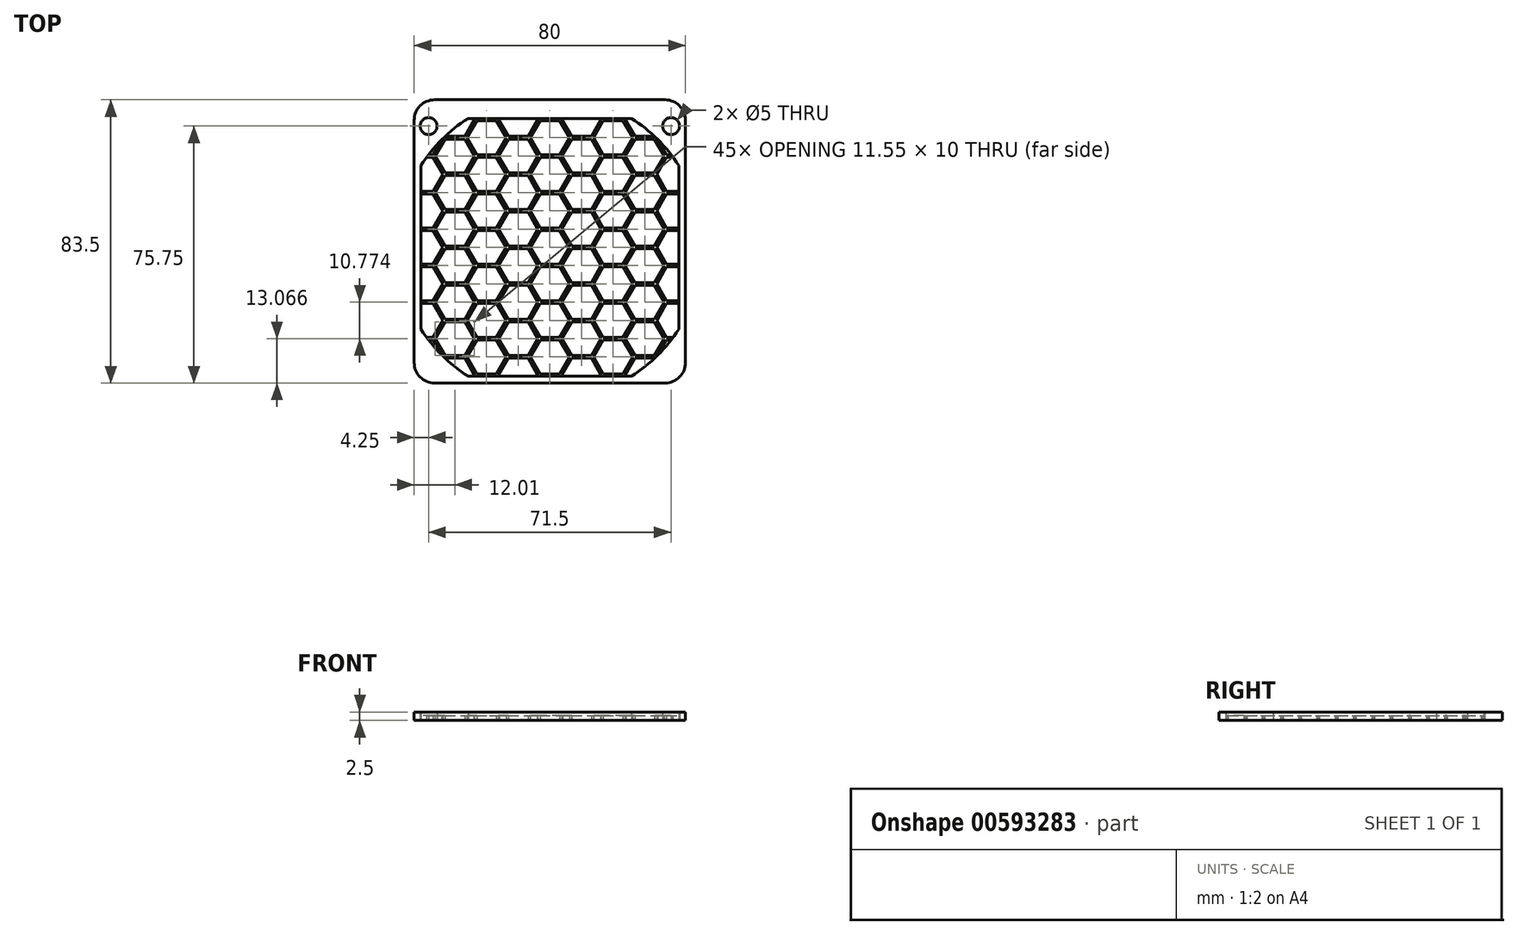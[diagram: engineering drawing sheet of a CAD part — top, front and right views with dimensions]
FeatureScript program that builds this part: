
annotation { "Feature Type Name" : "Feature", "Feature Type Description" : "" }
export const myFeature = defineFeature(function(context is Context, id is Id, definition is map)
    precondition{}
    {
        {
            var Q0;
            Q0=qCreatedBy(makeId("Top.planeOp"),FACE);
            var sketch = newSketch(context, id + "F0", { "sketchPlane" : qUnion([Q0]), "disableImprinting" : false});
            skPoint(sketch, "E0.1.2.4", {"position": v(-32.32, -29.43) * mm});
            skLineSegment(sketch, "E0.1.2.6", {"start": v(-35.76, -27.32) * mm, "end": v(-34.43, -27.32) * mm});
            skLineSegment(sketch, "E0.1.2.10", {"start": v(-34.43, -27.32) * mm, "end": v(-31.86, -31.78) * mm});
            skPoint(sketch, "E0.1.3.1", {"position": v(-37.32, -21.55) * mm});
            skPoint(sketch, "E0.1.3.4", {"position": v(-32.32, -18.66) * mm});
            skLineSegment(sketch, "E0.1.3.6", {"start": v(-38, -16.55) * mm, "end": v(-34.43, -16.55) * mm});
            skLineSegment(sketch, "E0.1.3.10", {"start": v(-34.43, -16.55) * mm, "end": v(-31.55, -21.55) * mm});
            skLineSegment(sketch, "E0.1.3.13", {"start": v(-31.55, -21.55) * mm, "end": v(-34.43, -26.55) * mm});
            skLineSegment(sketch, "E0.1.3.16", {"start": v(-34.43, -26.55) * mm, "end": v(-36.34, -26.55) * mm});
            skPoint(sketch, "E0.1.3.18", {"position": v(-37.32, -16.55) * mm});
            skPoint(sketch, "E0.1.4.1", {"position": v(-37.32, -10.77) * mm});
            skPoint(sketch, "E0.1.4.4", {"position": v(-32.32, -7.89) * mm});
            skLineSegment(sketch, "E0.1.4.6", {"start": v(-38, -5.77) * mm, "end": v(-34.43, -5.77) * mm});
            skLineSegment(sketch, "E0.1.4.10", {"start": v(-34.43, -5.77) * mm, "end": v(-31.55, -10.77) * mm});
            skLineSegment(sketch, "E0.1.4.13", {"start": v(-31.55, -10.77) * mm, "end": v(-34.43, -15.77) * mm});
            skLineSegment(sketch, "E0.1.4.16", {"start": v(-34.43, -15.77) * mm, "end": v(-38, -15.77) * mm});
            skPoint(sketch, "E0.1.4.18", {"position": v(-37.32, -5.77) * mm});
            skPoint(sketch, "E0.1.5.1", {"position": v(-37.32, 0) * mm});
            skPoint(sketch, "E0.1.5.4", {"position": v(-32.32, 2.89) * mm});
            skLineSegment(sketch, "E0.1.5.6", {"start": v(-38, 5) * mm, "end": v(-34.43, 5) * mm});
            skLineSegment(sketch, "E0.1.5.10", {"start": v(-34.43, 5) * mm, "end": v(-31.55, 0) * mm});
            skLineSegment(sketch, "E0.1.5.13", {"start": v(-31.55, 0) * mm, "end": v(-34.43, -5) * mm});
            skLineSegment(sketch, "E0.1.5.16", {"start": v(-34.43, -5) * mm, "end": v(-38, -5) * mm});
            skPoint(sketch, "E0.1.5.18", {"position": v(-37.32, 5) * mm});
            skPoint(sketch, "E0.1.6.1", {"position": v(-37.32, 10.77) * mm});
            skPoint(sketch, "E0.1.6.4", {"position": v(-32.32, 13.66) * mm});
            skLineSegment(sketch, "E0.1.6.6", {"start": v(-38, 15.77) * mm, "end": v(-34.43, 15.77) * mm});
            skLineSegment(sketch, "E0.1.6.10", {"start": v(-34.43, 15.77) * mm, "end": v(-31.55, 10.77) * mm});
            skLineSegment(sketch, "E0.1.6.13", {"start": v(-31.55, 10.77) * mm, "end": v(-34.43, 5.77) * mm});
            skLineSegment(sketch, "E0.1.6.16", {"start": v(-34.43, 5.77) * mm, "end": v(-38, 5.77) * mm});
            skPoint(sketch, "E0.1.6.18", {"position": v(-37.32, 15.77) * mm});
            skPoint(sketch, "E0.1.7.1", {"position": v(-37.32, 21.55) * mm});
            skPoint(sketch, "E0.1.7.4", {"position": v(-32.32, 24.43) * mm});
            skLineSegment(sketch, "E0.1.7.6", {"start": v(-36.34, 26.55) * mm, "end": v(-34.43, 26.55) * mm});
            skLineSegment(sketch, "E0.1.7.10", {"start": v(-34.43, 26.55) * mm, "end": v(-31.55, 21.55) * mm});
            skLineSegment(sketch, "E0.1.7.13", {"start": v(-31.55, 21.55) * mm, "end": v(-34.43, 16.55) * mm});
            skLineSegment(sketch, "E0.1.7.16", {"start": v(-34.43, 16.55) * mm, "end": v(-38, 16.55) * mm});
            skLineSegment(sketch, "E0.1.8.13", {"start": v(-31.86, 31.78) * mm, "end": v(-34.43, 27.32) * mm});
            skLineSegment(sketch, "E0.1.8.16", {"start": v(-34.43, 27.32) * mm, "end": v(-35.76, 27.32) * mm});
            skPoint(sketch, "E0.2.1.18", {"position": v(-18.66, -38.1) * mm});
            skLineSegment(sketch, "E0.2.2.0", {"start": v(-24.43, -32.32) * mm, "end": v(-21.55, -27.32) * mm});
            skPoint(sketch, "E0.2.2.1", {"position": v(-18.66, -32.32) * mm});
            skLineSegment(sketch, "E0.2.2.3", {"start": v(-25.1, -32.7) * mm, "end": v(-22.22, -37.7) * mm});
            skPoint(sketch, "E0.2.2.4", {"position": v(-13.66, -29.43) * mm});
            skLineSegment(sketch, "E0.2.2.5", {"start": v(-30.9, -32.7) * mm, "end": v(-25.1, -32.7) * mm});
            skLineSegment(sketch, "E0.2.2.6", {"start": v(-21.55, -27.32) * mm, "end": v(-15.77, -27.32) * mm});
            skLineSegment(sketch, "E0.2.2.10", {"start": v(-15.77, -27.32) * mm, "end": v(-12.89, -32.32) * mm});
            skLineSegment(sketch, "E0.2.2.12", {"start": v(-22.22, -37.7) * mm, "end": v(-22.39, -38) * mm});
            skLineSegment(sketch, "E0.2.2.13", {"start": v(-12.89, -32.32) * mm, "end": v(-15.77, -37.32) * mm});
            skPoint(sketch, "E0.2.2.14", {"position": v(-23, -34.82) * mm});
            skLineSegment(sketch, "E0.2.2.15", {"start": v(-21.55, -37.32) * mm, "end": v(-24.43, -32.32) * mm});
            skLineSegment(sketch, "E0.2.2.16", {"start": v(-15.77, -37.32) * mm, "end": v(-21.55, -37.32) * mm});
            skPoint(sketch, "E0.2.2.17", {"position": v(-28, -32.7) * mm});
            skPoint(sketch, "E0.2.2.18", {"position": v(-18.66, -27.32) * mm});
            skPoint(sketch, "E0.2.2.19", {"position": v(-23, -34.82) * mm});
            skLineSegment(sketch, "E0.2.3.0", {"start": v(-24.43, -21.55) * mm, "end": v(-21.55, -16.55) * mm});
            skPoint(sketch, "E0.2.3.1", {"position": v(-18.66, -21.55) * mm});
            skPoint(sketch, "E0.2.3.2", {"position": v(-28, -26.93) * mm});
            skLineSegment(sketch, "E0.2.3.3", {"start": v(-25.1, -21.93) * mm, "end": v(-22.22, -26.93) * mm});
            skPoint(sketch, "E0.2.3.4", {"position": v(-13.66, -18.66) * mm});
            skLineSegment(sketch, "E0.2.3.5", {"start": v(-30.88, -21.93) * mm, "end": v(-25.1, -21.93) * mm});
            skLineSegment(sketch, "E0.2.3.6", {"start": v(-21.55, -16.55) * mm, "end": v(-15.77, -16.55) * mm});
            skLineSegment(sketch, "E0.2.3.7", {"start": v(-25.1, -31.93) * mm, "end": v(-30.88, -31.93) * mm});
            skPoint(sketch, "E0.2.3.8", {"position": v(-32.32, -29.43) * mm});
            skLineSegment(sketch, "E0.2.3.9", {"start": v(-30.88, -31.93) * mm, "end": v(-33.76, -26.93) * mm});
            skLineSegment(sketch, "E0.2.3.10", {"start": v(-15.77, -16.55) * mm, "end": v(-12.89, -21.55) * mm});
            skLineSegment(sketch, "E0.2.3.11", {"start": v(-33.76, -26.93) * mm, "end": v(-30.88, -21.93) * mm});
            skLineSegment(sketch, "E0.2.3.12", {"start": v(-22.22, -26.93) * mm, "end": v(-25.1, -31.93) * mm});
            skLineSegment(sketch, "E0.2.3.13", {"start": v(-12.89, -21.55) * mm, "end": v(-15.77, -26.55) * mm});
            skPoint(sketch, "E0.2.3.14", {"position": v(-23, -24.05) * mm});
            skLineSegment(sketch, "E0.2.3.15", {"start": v(-21.55, -26.55) * mm, "end": v(-24.43, -21.55) * mm});
            skLineSegment(sketch, "E0.2.3.16", {"start": v(-15.77, -26.55) * mm, "end": v(-21.55, -26.55) * mm});
            skPoint(sketch, "E0.2.3.17", {"position": v(-28, -21.93) * mm});
            skPoint(sketch, "E0.2.3.18", {"position": v(-18.66, -16.55) * mm});
            skPoint(sketch, "E0.2.3.19", {"position": v(-23, -24.05) * mm});
            skLineSegment(sketch, "E0.2.4.0", {"start": v(-24.43, -10.77) * mm, "end": v(-21.55, -5.77) * mm});
            skPoint(sketch, "E0.2.4.1", {"position": v(-18.66, -10.77) * mm});
            skPoint(sketch, "E0.2.4.2", {"position": v(-28, -16.16) * mm});
            skLineSegment(sketch, "E0.2.4.3", {"start": v(-25.1, -11.16) * mm, "end": v(-22.22, -16.16) * mm});
            skPoint(sketch, "E0.2.4.4", {"position": v(-13.66, -7.89) * mm});
            skLineSegment(sketch, "E0.2.4.5", {"start": v(-30.88, -11.16) * mm, "end": v(-25.1, -11.16) * mm});
            skLineSegment(sketch, "E0.2.4.6", {"start": v(-21.55, -5.77) * mm, "end": v(-15.77, -5.77) * mm});
            skLineSegment(sketch, "E0.2.4.7", {"start": v(-25.1, -21.16) * mm, "end": v(-30.88, -21.16) * mm});
            skPoint(sketch, "E0.2.4.8", {"position": v(-32.32, -18.66) * mm});
            skLineSegment(sketch, "E0.2.4.9", {"start": v(-30.88, -21.16) * mm, "end": v(-33.76, -16.16) * mm});
            skLineSegment(sketch, "E0.2.4.10", {"start": v(-15.77, -5.77) * mm, "end": v(-12.89, -10.77) * mm});
            skLineSegment(sketch, "E0.2.4.11", {"start": v(-33.76, -16.16) * mm, "end": v(-30.88, -11.16) * mm});
            skLineSegment(sketch, "E0.2.4.12", {"start": v(-22.22, -16.16) * mm, "end": v(-25.1, -21.16) * mm});
            skLineSegment(sketch, "E0.2.4.13", {"start": v(-12.89, -10.77) * mm, "end": v(-15.77, -15.77) * mm});
            skPoint(sketch, "E0.2.4.14", {"position": v(-23, -13.27) * mm});
            skLineSegment(sketch, "E0.2.4.15", {"start": v(-21.55, -15.77) * mm, "end": v(-24.43, -10.77) * mm});
            skLineSegment(sketch, "E0.2.4.16", {"start": v(-15.77, -15.77) * mm, "end": v(-21.55, -15.77) * mm});
            skPoint(sketch, "E0.2.4.17", {"position": v(-28, -11.16) * mm});
            skPoint(sketch, "E0.2.4.18", {"position": v(-18.66, -5.77) * mm});
            skPoint(sketch, "E0.2.4.19", {"position": v(-23, -13.27) * mm});
            skLineSegment(sketch, "E0.2.5.0", {"start": v(-24.43, 0) * mm, "end": v(-21.55, 5) * mm});
            skPoint(sketch, "E0.2.5.1", {"position": v(-18.66, 0) * mm});
            skPoint(sketch, "E0.2.5.2", {"position": v(-28, -5.39) * mm});
            skLineSegment(sketch, "E0.2.5.3", {"start": v(-25.1, -0.39) * mm, "end": v(-22.22, -5.39) * mm});
            skPoint(sketch, "E0.2.5.4", {"position": v(-13.66, 2.89) * mm});
            skLineSegment(sketch, "E0.2.5.5", {"start": v(-30.88, -0.39) * mm, "end": v(-25.1, -0.39) * mm});
            skLineSegment(sketch, "E0.2.5.6", {"start": v(-21.55, 5) * mm, "end": v(-15.77, 5) * mm});
            skLineSegment(sketch, "E0.2.5.7", {"start": v(-25.1, -10.39) * mm, "end": v(-30.88, -10.39) * mm});
            skPoint(sketch, "E0.2.5.8", {"position": v(-32.32, -7.89) * mm});
            skLineSegment(sketch, "E0.2.5.9", {"start": v(-30.88, -10.39) * mm, "end": v(-33.76, -5.39) * mm});
            skLineSegment(sketch, "E0.2.5.10", {"start": v(-15.77, 5) * mm, "end": v(-12.89, 0) * mm});
            skLineSegment(sketch, "E0.2.5.11", {"start": v(-33.76, -5.39) * mm, "end": v(-30.88, -0.39) * mm});
            skLineSegment(sketch, "E0.2.5.12", {"start": v(-22.22, -5.39) * mm, "end": v(-25.1, -10.39) * mm});
            skLineSegment(sketch, "E0.2.5.13", {"start": v(-12.89, 0) * mm, "end": v(-15.77, -5) * mm});
            skPoint(sketch, "E0.2.5.14", {"position": v(-23, -2.5) * mm});
            skLineSegment(sketch, "E0.2.5.15", {"start": v(-21.55, -5) * mm, "end": v(-24.43, 0) * mm});
            skLineSegment(sketch, "E0.2.5.16", {"start": v(-15.77, -5) * mm, "end": v(-21.55, -5) * mm});
            skPoint(sketch, "E0.2.5.17", {"position": v(-28, -0.39) * mm});
            skPoint(sketch, "E0.2.5.18", {"position": v(-18.66, 5) * mm});
            skPoint(sketch, "E0.2.5.19", {"position": v(-23, -2.5) * mm});
            skLineSegment(sketch, "E0.2.6.0", {"start": v(-24.43, 10.77) * mm, "end": v(-21.55, 15.77) * mm});
            skPoint(sketch, "E0.2.6.1", {"position": v(-18.66, 10.77) * mm});
            skPoint(sketch, "E0.2.6.2", {"position": v(-28, 5.39) * mm});
            skLineSegment(sketch, "E0.2.6.3", {"start": v(-25.1, 10.39) * mm, "end": v(-22.22, 5.39) * mm});
            skPoint(sketch, "E0.2.6.4", {"position": v(-13.66, 13.66) * mm});
            skLineSegment(sketch, "E0.2.6.5", {"start": v(-30.88, 10.39) * mm, "end": v(-25.1, 10.39) * mm});
            skLineSegment(sketch, "E0.2.6.6", {"start": v(-21.55, 15.77) * mm, "end": v(-15.77, 15.77) * mm});
            skLineSegment(sketch, "E0.2.6.7", {"start": v(-25.1, 0.39) * mm, "end": v(-30.88, 0.39) * mm});
            skPoint(sketch, "E0.2.6.8", {"position": v(-32.32, 2.89) * mm});
            skLineSegment(sketch, "E0.2.6.9", {"start": v(-30.88, 0.39) * mm, "end": v(-33.76, 5.39) * mm});
            skLineSegment(sketch, "E0.2.6.10", {"start": v(-15.77, 15.77) * mm, "end": v(-12.89, 10.77) * mm});
            skLineSegment(sketch, "E0.2.6.11", {"start": v(-33.76, 5.39) * mm, "end": v(-30.88, 10.39) * mm});
            skLineSegment(sketch, "E0.2.6.12", {"start": v(-22.22, 5.39) * mm, "end": v(-25.1, 0.39) * mm});
            skLineSegment(sketch, "E0.2.6.13", {"start": v(-12.89, 10.77) * mm, "end": v(-15.77, 5.77) * mm});
            skPoint(sketch, "E0.2.6.14", {"position": v(-23, 8.27) * mm});
            skLineSegment(sketch, "E0.2.6.15", {"start": v(-21.55, 5.77) * mm, "end": v(-24.43, 10.77) * mm});
            skLineSegment(sketch, "E0.2.6.16", {"start": v(-15.77, 5.77) * mm, "end": v(-21.55, 5.77) * mm});
            skPoint(sketch, "E0.2.6.17", {"position": v(-28, 10.39) * mm});
            skPoint(sketch, "E0.2.6.18", {"position": v(-18.66, 15.77) * mm});
            skPoint(sketch, "E0.2.6.19", {"position": v(-23, 8.27) * mm});
            skLineSegment(sketch, "E0.2.7.0", {"start": v(-24.43, 21.55) * mm, "end": v(-21.55, 26.55) * mm});
            skPoint(sketch, "E0.2.7.1", {"position": v(-18.66, 21.55) * mm});
            skPoint(sketch, "E0.2.7.2", {"position": v(-28, 16.16) * mm});
            skLineSegment(sketch, "E0.2.7.3", {"start": v(-25.1, 21.16) * mm, "end": v(-22.22, 16.16) * mm});
            skPoint(sketch, "E0.2.7.4", {"position": v(-13.66, 24.43) * mm});
            skLineSegment(sketch, "E0.2.7.5", {"start": v(-30.88, 21.16) * mm, "end": v(-25.1, 21.16) * mm});
            skLineSegment(sketch, "E0.2.7.6", {"start": v(-21.55, 26.55) * mm, "end": v(-15.77, 26.55) * mm});
            skLineSegment(sketch, "E0.2.7.7", {"start": v(-25.1, 11.16) * mm, "end": v(-30.88, 11.16) * mm});
            skPoint(sketch, "E0.2.7.8", {"position": v(-32.32, 13.66) * mm});
            skLineSegment(sketch, "E0.2.7.9", {"start": v(-30.88, 11.16) * mm, "end": v(-33.76, 16.16) * mm});
            skLineSegment(sketch, "E0.2.7.10", {"start": v(-15.77, 26.55) * mm, "end": v(-12.89, 21.55) * mm});
            skLineSegment(sketch, "E0.2.7.11", {"start": v(-33.76, 16.16) * mm, "end": v(-30.88, 21.16) * mm});
            skLineSegment(sketch, "E0.2.7.12", {"start": v(-22.22, 16.16) * mm, "end": v(-25.1, 11.16) * mm});
            skLineSegment(sketch, "E0.2.7.13", {"start": v(-12.89, 21.55) * mm, "end": v(-15.77, 16.55) * mm});
            skPoint(sketch, "E0.2.7.14", {"position": v(-23, 19.05) * mm});
            skLineSegment(sketch, "E0.2.7.15", {"start": v(-21.55, 16.55) * mm, "end": v(-24.43, 21.55) * mm});
            skLineSegment(sketch, "E0.2.7.16", {"start": v(-15.77, 16.55) * mm, "end": v(-21.55, 16.55) * mm});
            skPoint(sketch, "E0.2.7.17", {"position": v(-28, 21.16) * mm});
            skPoint(sketch, "E0.2.7.18", {"position": v(-18.66, 26.55) * mm});
            skPoint(sketch, "E0.2.7.19", {"position": v(-23, 19.05) * mm});
            skLineSegment(sketch, "E0.2.8.0", {"start": v(-24.43, 32.32) * mm, "end": v(-21.55, 37.32) * mm});
            skPoint(sketch, "E0.2.8.1", {"position": v(-18.66, 32.32) * mm});
            skPoint(sketch, "E0.2.8.2", {"position": v(-28, 26.93) * mm});
            skLineSegment(sketch, "E0.2.8.3", {"start": v(-25.1, 31.93) * mm, "end": v(-22.22, 26.93) * mm});
            skPoint(sketch, "E0.2.8.4", {"position": v(-13.66, 35.2) * mm});
            skLineSegment(sketch, "E0.2.8.5", {"start": v(-30.88, 31.93) * mm, "end": v(-25.1, 31.93) * mm});
            skLineSegment(sketch, "E0.2.8.6", {"start": v(-21.55, 37.32) * mm, "end": v(-15.77, 37.32) * mm});
            skLineSegment(sketch, "E0.2.8.7", {"start": v(-25.1, 21.93) * mm, "end": v(-30.88, 21.93) * mm});
            skPoint(sketch, "E0.2.8.8", {"position": v(-32.32, 24.43) * mm});
            skLineSegment(sketch, "E0.2.8.9", {"start": v(-30.88, 21.93) * mm, "end": v(-33.76, 26.93) * mm});
            skLineSegment(sketch, "E0.2.8.10", {"start": v(-15.77, 37.32) * mm, "end": v(-12.89, 32.32) * mm});
            skLineSegment(sketch, "E0.2.8.11", {"start": v(-33.76, 26.93) * mm, "end": v(-30.88, 31.93) * mm});
            skLineSegment(sketch, "E0.2.8.12", {"start": v(-22.22, 26.93) * mm, "end": v(-25.1, 21.93) * mm});
            skLineSegment(sketch, "E0.2.8.13", {"start": v(-12.89, 32.32) * mm, "end": v(-15.77, 27.32) * mm});
            skPoint(sketch, "E0.2.8.14", {"position": v(-23, 29.82) * mm});
            skLineSegment(sketch, "E0.2.8.15", {"start": v(-21.55, 27.32) * mm, "end": v(-24.43, 32.32) * mm});
            skLineSegment(sketch, "E0.2.8.16", {"start": v(-15.77, 27.32) * mm, "end": v(-21.55, 27.32) * mm});
            skPoint(sketch, "E0.2.8.17", {"position": v(-28, 31.93) * mm});
            skPoint(sketch, "E0.2.8.18", {"position": v(-18.66, 37.32) * mm});
            skPoint(sketch, "E0.2.8.19", {"position": v(-23, 29.82) * mm});
            skLineSegment(sketch, "E0.2.9.3", {"start": v(-22.39, 38) * mm, "end": v(-22.22, 37.7) * mm});
            skLineSegment(sketch, "E0.2.9.7", {"start": v(-25.1, 32.7) * mm, "end": v(-30.9, 32.7) * mm});
            skLineSegment(sketch, "E0.2.9.12", {"start": v(-22.22, 37.7) * mm, "end": v(-25.1, 32.7) * mm});
            skPoint(sketch, "E0.3.1.18", {"position": v(0, -38.1) * mm});
            skLineSegment(sketch, "E0.3.2.0", {"start": v(-5.77, -32.32) * mm, "end": v(-2.89, -27.32) * mm});
            skPoint(sketch, "E0.3.2.1", {"position": v(0, -32.32) * mm});
            skPoint(sketch, "E0.3.2.2", {"position": v(-9.33, -37.7) * mm});
            skLineSegment(sketch, "E0.3.2.3", {"start": v(-6.44, -32.7) * mm, "end": v(-3.56, -37.7) * mm});
            skPoint(sketch, "E0.3.2.4", {"position": v(5, -29.43) * mm});
            skLineSegment(sketch, "E0.3.2.5", {"start": v(-12.22, -32.7) * mm, "end": v(-6.44, -32.7) * mm});
            skLineSegment(sketch, "E0.3.2.6", {"start": v(-2.89, -27.32) * mm, "end": v(2.89, -27.32) * mm});
            skLineSegment(sketch, "E0.3.2.9", {"start": v(-14.93, -38) * mm, "end": v(-15.1, -37.7) * mm});
            skLineSegment(sketch, "E0.3.2.10", {"start": v(2.89, -27.32) * mm, "end": v(5.77, -32.32) * mm});
            skLineSegment(sketch, "E0.3.2.11", {"start": v(-15.1, -37.7) * mm, "end": v(-12.22, -32.7) * mm});
            skLineSegment(sketch, "E0.3.2.12", {"start": v(-3.56, -37.7) * mm, "end": v(-3.73, -38) * mm});
            skLineSegment(sketch, "E0.3.2.13", {"start": v(5.77, -32.32) * mm, "end": v(2.89, -37.32) * mm});
            skPoint(sketch, "E0.3.2.14", {"position": v(-4.33, -34.82) * mm});
            skLineSegment(sketch, "E0.3.2.15", {"start": v(-2.89, -37.32) * mm, "end": v(-5.77, -32.32) * mm});
            skLineSegment(sketch, "E0.3.2.16", {"start": v(2.89, -37.32) * mm, "end": v(-2.89, -37.32) * mm});
            skPoint(sketch, "E0.3.2.17", {"position": v(-9.33, -32.7) * mm});
            skPoint(sketch, "E0.3.2.18", {"position": v(0, -27.32) * mm});
            skPoint(sketch, "E0.3.2.19", {"position": v(-4.33, -34.82) * mm});
            skLineSegment(sketch, "E0.3.3.0", {"start": v(-5.77, -21.55) * mm, "end": v(-2.89, -16.55) * mm});
            skPoint(sketch, "E0.3.3.1", {"position": v(0, -21.55) * mm});
            skPoint(sketch, "E0.3.3.2", {"position": v(-9.33, -26.93) * mm});
            skLineSegment(sketch, "E0.3.3.3", {"start": v(-6.44, -21.93) * mm, "end": v(-3.56, -26.93) * mm});
            skPoint(sketch, "E0.3.3.4", {"position": v(5, -18.66) * mm});
            skLineSegment(sketch, "E0.3.3.5", {"start": v(-12.22, -21.93) * mm, "end": v(-6.44, -21.93) * mm});
            skLineSegment(sketch, "E0.3.3.6", {"start": v(-2.89, -16.55) * mm, "end": v(2.89, -16.55) * mm});
            skLineSegment(sketch, "E0.3.3.7", {"start": v(-6.44, -31.93) * mm, "end": v(-12.22, -31.93) * mm});
            skPoint(sketch, "E0.3.3.8", {"position": v(-13.66, -29.43) * mm});
            skLineSegment(sketch, "E0.3.3.9", {"start": v(-12.22, -31.93) * mm, "end": v(-15.1, -26.93) * mm});
            skLineSegment(sketch, "E0.3.3.10", {"start": v(2.89, -16.55) * mm, "end": v(5.77, -21.55) * mm});
            skLineSegment(sketch, "E0.3.3.11", {"start": v(-15.1, -26.93) * mm, "end": v(-12.22, -21.93) * mm});
            skLineSegment(sketch, "E0.3.3.12", {"start": v(-3.56, -26.93) * mm, "end": v(-6.44, -31.93) * mm});
            skLineSegment(sketch, "E0.3.3.13", {"start": v(5.77, -21.55) * mm, "end": v(2.89, -26.55) * mm});
            skPoint(sketch, "E0.3.3.14", {"position": v(-4.33, -24.05) * mm});
            skLineSegment(sketch, "E0.3.3.15", {"start": v(-2.89, -26.55) * mm, "end": v(-5.77, -21.55) * mm});
            skLineSegment(sketch, "E0.3.3.16", {"start": v(2.89, -26.55) * mm, "end": v(-2.89, -26.55) * mm});
            skPoint(sketch, "E0.3.3.17", {"position": v(-9.33, -21.93) * mm});
            skPoint(sketch, "E0.3.3.18", {"position": v(0, -16.55) * mm});
            skPoint(sketch, "E0.3.3.19", {"position": v(-4.33, -24.05) * mm});
            skLineSegment(sketch, "E0.3.4.0", {"start": v(-5.77, -10.77) * mm, "end": v(-2.89, -5.77) * mm});
            skPoint(sketch, "E0.3.4.1", {"position": v(0, -10.77) * mm});
            skPoint(sketch, "E0.3.4.2", {"position": v(-9.33, -16.16) * mm});
            skLineSegment(sketch, "E0.3.4.3", {"start": v(-6.44, -11.16) * mm, "end": v(-3.56, -16.16) * mm});
            skPoint(sketch, "E0.3.4.4", {"position": v(5, -7.89) * mm});
            skLineSegment(sketch, "E0.3.4.5", {"start": v(-12.22, -11.16) * mm, "end": v(-6.44, -11.16) * mm});
            skLineSegment(sketch, "E0.3.4.6", {"start": v(-2.89, -5.77) * mm, "end": v(2.89, -5.77) * mm});
            skLineSegment(sketch, "E0.3.4.7", {"start": v(-6.44, -21.16) * mm, "end": v(-12.22, -21.16) * mm});
            skPoint(sketch, "E0.3.4.8", {"position": v(-13.66, -18.66) * mm});
            skLineSegment(sketch, "E0.3.4.9", {"start": v(-12.22, -21.16) * mm, "end": v(-15.1, -16.16) * mm});
            skLineSegment(sketch, "E0.3.4.10", {"start": v(2.89, -5.77) * mm, "end": v(5.77, -10.77) * mm});
            skLineSegment(sketch, "E0.3.4.11", {"start": v(-15.1, -16.16) * mm, "end": v(-12.22, -11.16) * mm});
            skLineSegment(sketch, "E0.3.4.12", {"start": v(-3.56, -16.16) * mm, "end": v(-6.44, -21.16) * mm});
            skLineSegment(sketch, "E0.3.4.13", {"start": v(5.77, -10.77) * mm, "end": v(2.89, -15.77) * mm});
            skPoint(sketch, "E0.3.4.14", {"position": v(-4.33, -13.27) * mm});
            skLineSegment(sketch, "E0.3.4.15", {"start": v(-2.89, -15.77) * mm, "end": v(-5.77, -10.77) * mm});
            skLineSegment(sketch, "E0.3.4.16", {"start": v(2.89, -15.77) * mm, "end": v(-2.89, -15.77) * mm});
            skPoint(sketch, "E0.3.4.17", {"position": v(-9.33, -11.16) * mm});
            skPoint(sketch, "E0.3.4.18", {"position": v(0, -5.77) * mm});
            skPoint(sketch, "E0.3.4.19", {"position": v(-4.33, -13.27) * mm});
            skLineSegment(sketch, "E0.3.5.0", {"start": v(-5.77, 0) * mm, "end": v(-2.89, 5) * mm});
            skPoint(sketch, "E0.3.5.1", {"position": v(0, 0) * mm});
            skPoint(sketch, "E0.3.5.2", {"position": v(-9.33, -5.39) * mm});
            skLineSegment(sketch, "E0.3.5.3", {"start": v(-6.44, -0.39) * mm, "end": v(-3.56, -5.39) * mm});
            skPoint(sketch, "E0.3.5.4", {"position": v(5, 2.89) * mm});
            skLineSegment(sketch, "E0.3.5.5", {"start": v(-12.22, -0.39) * mm, "end": v(-6.44, -0.39) * mm});
            skLineSegment(sketch, "E0.3.5.6", {"start": v(-2.89, 5) * mm, "end": v(2.89, 5) * mm});
            skLineSegment(sketch, "E0.3.5.7", {"start": v(-6.44, -10.39) * mm, "end": v(-12.22, -10.39) * mm});
            skPoint(sketch, "E0.3.5.8", {"position": v(-13.66, -7.89) * mm});
            skLineSegment(sketch, "E0.3.5.9", {"start": v(-12.22, -10.39) * mm, "end": v(-15.1, -5.39) * mm});
            skLineSegment(sketch, "E0.3.5.10", {"start": v(2.89, 5) * mm, "end": v(5.77, 0) * mm});
            skLineSegment(sketch, "E0.3.5.11", {"start": v(-15.1, -5.39) * mm, "end": v(-12.22, -0.39) * mm});
            skLineSegment(sketch, "E0.3.5.12", {"start": v(-3.56, -5.39) * mm, "end": v(-6.44, -10.39) * mm});
            skLineSegment(sketch, "E0.3.5.13", {"start": v(5.77, 0) * mm, "end": v(2.89, -5) * mm});
            skPoint(sketch, "E0.3.5.14", {"position": v(-4.33, -2.5) * mm});
            skLineSegment(sketch, "E0.3.5.15", {"start": v(-2.89, -5) * mm, "end": v(-5.77, 0) * mm});
            skLineSegment(sketch, "E0.3.5.16", {"start": v(2.89, -5) * mm, "end": v(-2.89, -5) * mm});
            skPoint(sketch, "E0.3.5.17", {"position": v(-9.33, -0.39) * mm});
            skPoint(sketch, "E0.3.5.18", {"position": v(0, 5) * mm});
            skPoint(sketch, "E0.3.5.19", {"position": v(-4.33, -2.5) * mm});
            skLineSegment(sketch, "E0.3.6.0", {"start": v(-5.77, 10.77) * mm, "end": v(-2.89, 15.77) * mm});
            skPoint(sketch, "E0.3.6.1", {"position": v(0, 10.77) * mm});
            skPoint(sketch, "E0.3.6.2", {"position": v(-9.33, 5.39) * mm});
            skLineSegment(sketch, "E0.3.6.3", {"start": v(-6.44, 10.39) * mm, "end": v(-3.56, 5.39) * mm});
            skPoint(sketch, "E0.3.6.4", {"position": v(5, 13.66) * mm});
            skLineSegment(sketch, "E0.3.6.5", {"start": v(-12.22, 10.39) * mm, "end": v(-6.44, 10.39) * mm});
            skLineSegment(sketch, "E0.3.6.6", {"start": v(-2.89, 15.77) * mm, "end": v(2.89, 15.77) * mm});
            skLineSegment(sketch, "E0.3.6.7", {"start": v(-6.44, 0.39) * mm, "end": v(-12.22, 0.39) * mm});
            skPoint(sketch, "E0.3.6.8", {"position": v(-13.66, 2.89) * mm});
            skLineSegment(sketch, "E0.3.6.9", {"start": v(-12.22, 0.39) * mm, "end": v(-15.1, 5.39) * mm});
            skLineSegment(sketch, "E0.3.6.10", {"start": v(2.89, 15.77) * mm, "end": v(5.77, 10.77) * mm});
            skLineSegment(sketch, "E0.3.6.11", {"start": v(-15.1, 5.39) * mm, "end": v(-12.22, 10.39) * mm});
            skLineSegment(sketch, "E0.3.6.12", {"start": v(-3.56, 5.39) * mm, "end": v(-6.44, 0.39) * mm});
            skLineSegment(sketch, "E0.3.6.13", {"start": v(5.77, 10.77) * mm, "end": v(2.89, 5.77) * mm});
            skPoint(sketch, "E0.3.6.14", {"position": v(-4.33, 8.27) * mm});
            skLineSegment(sketch, "E0.3.6.15", {"start": v(-2.89, 5.77) * mm, "end": v(-5.77, 10.77) * mm});
            skLineSegment(sketch, "E0.3.6.16", {"start": v(2.89, 5.77) * mm, "end": v(-2.89, 5.77) * mm});
            skPoint(sketch, "E0.3.6.17", {"position": v(-9.33, 10.39) * mm});
            skPoint(sketch, "E0.3.6.18", {"position": v(0, 15.77) * mm});
            skPoint(sketch, "E0.3.6.19", {"position": v(-4.33, 8.27) * mm});
            skLineSegment(sketch, "E0.3.7.0", {"start": v(-5.77, 21.55) * mm, "end": v(-2.89, 26.55) * mm});
            skPoint(sketch, "E0.3.7.1", {"position": v(0, 21.55) * mm});
            skPoint(sketch, "E0.3.7.2", {"position": v(-9.33, 16.16) * mm});
            skLineSegment(sketch, "E0.3.7.3", {"start": v(-6.44, 21.16) * mm, "end": v(-3.56, 16.16) * mm});
            skPoint(sketch, "E0.3.7.4", {"position": v(5, 24.43) * mm});
            skLineSegment(sketch, "E0.3.7.5", {"start": v(-12.22, 21.16) * mm, "end": v(-6.44, 21.16) * mm});
            skLineSegment(sketch, "E0.3.7.6", {"start": v(-2.89, 26.55) * mm, "end": v(2.89, 26.55) * mm});
            skLineSegment(sketch, "E0.3.7.7", {"start": v(-6.44, 11.16) * mm, "end": v(-12.22, 11.16) * mm});
            skPoint(sketch, "E0.3.7.8", {"position": v(-13.66, 13.66) * mm});
            skLineSegment(sketch, "E0.3.7.9", {"start": v(-12.22, 11.16) * mm, "end": v(-15.1, 16.16) * mm});
            skLineSegment(sketch, "E0.3.7.10", {"start": v(2.89, 26.55) * mm, "end": v(5.77, 21.55) * mm});
            skLineSegment(sketch, "E0.3.7.11", {"start": v(-15.1, 16.16) * mm, "end": v(-12.22, 21.16) * mm});
            skLineSegment(sketch, "E0.3.7.12", {"start": v(-3.56, 16.16) * mm, "end": v(-6.44, 11.16) * mm});
            skLineSegment(sketch, "E0.3.7.13", {"start": v(5.77, 21.55) * mm, "end": v(2.89, 16.55) * mm});
            skPoint(sketch, "E0.3.7.14", {"position": v(-4.33, 19.05) * mm});
            skLineSegment(sketch, "E0.3.7.15", {"start": v(-2.89, 16.55) * mm, "end": v(-5.77, 21.55) * mm});
            skLineSegment(sketch, "E0.3.7.16", {"start": v(2.89, 16.55) * mm, "end": v(-2.89, 16.55) * mm});
            skPoint(sketch, "E0.3.7.17", {"position": v(-9.33, 21.16) * mm});
            skPoint(sketch, "E0.3.7.18", {"position": v(0, 26.55) * mm});
            skPoint(sketch, "E0.3.7.19", {"position": v(-4.33, 19.05) * mm});
            skLineSegment(sketch, "E0.3.8.0", {"start": v(-5.77, 32.32) * mm, "end": v(-2.89, 37.32) * mm});
            skPoint(sketch, "E0.3.8.1", {"position": v(0, 32.32) * mm});
            skPoint(sketch, "E0.3.8.2", {"position": v(-9.33, 26.93) * mm});
            skLineSegment(sketch, "E0.3.8.3", {"start": v(-6.44, 31.93) * mm, "end": v(-3.56, 26.93) * mm});
            skPoint(sketch, "E0.3.8.4", {"position": v(5, 35.2) * mm});
            skLineSegment(sketch, "E0.3.8.5", {"start": v(-12.22, 31.93) * mm, "end": v(-6.44, 31.93) * mm});
            skLineSegment(sketch, "E0.3.8.6", {"start": v(-2.89, 37.32) * mm, "end": v(2.89, 37.32) * mm});
            skLineSegment(sketch, "E0.3.8.7", {"start": v(-6.44, 21.93) * mm, "end": v(-12.22, 21.93) * mm});
            skPoint(sketch, "E0.3.8.8", {"position": v(-13.66, 24.43) * mm});
            skLineSegment(sketch, "E0.3.8.9", {"start": v(-12.22, 21.93) * mm, "end": v(-15.1, 26.93) * mm});
            skLineSegment(sketch, "E0.3.8.10", {"start": v(2.89, 37.32) * mm, "end": v(5.77, 32.32) * mm});
            skLineSegment(sketch, "E0.3.8.11", {"start": v(-15.1, 26.93) * mm, "end": v(-12.22, 31.93) * mm});
            skLineSegment(sketch, "E0.3.8.12", {"start": v(-3.56, 26.93) * mm, "end": v(-6.44, 21.93) * mm});
            skLineSegment(sketch, "E0.3.8.13", {"start": v(5.77, 32.32) * mm, "end": v(2.89, 27.32) * mm});
            skPoint(sketch, "E0.3.8.14", {"position": v(-4.33, 29.82) * mm});
            skLineSegment(sketch, "E0.3.8.15", {"start": v(-2.89, 27.32) * mm, "end": v(-5.77, 32.32) * mm});
            skLineSegment(sketch, "E0.3.8.16", {"start": v(2.89, 27.32) * mm, "end": v(-2.89, 27.32) * mm});
            skPoint(sketch, "E0.3.8.17", {"position": v(-9.33, 31.93) * mm});
            skPoint(sketch, "E0.3.8.18", {"position": v(0, 37.32) * mm});
            skPoint(sketch, "E0.3.8.19", {"position": v(-4.33, 29.82) * mm});
            skPoint(sketch, "E0.3.9.2", {"position": v(-9.33, 37.7) * mm});
            skLineSegment(sketch, "E0.3.9.3", {"start": v(-3.73, 38) * mm, "end": v(-3.56, 37.7) * mm});
            skLineSegment(sketch, "E0.3.9.7", {"start": v(-6.44, 32.7) * mm, "end": v(-12.22, 32.7) * mm});
            skPoint(sketch, "E0.3.9.8", {"position": v(-13.66, 35.2) * mm});
            skLineSegment(sketch, "E0.3.9.9", {"start": v(-12.22, 32.7) * mm, "end": v(-15.1, 37.7) * mm});
            skLineSegment(sketch, "E0.3.9.11", {"start": v(-15.1, 37.7) * mm, "end": v(-14.93, 38) * mm});
            skLineSegment(sketch, "E0.3.9.12", {"start": v(-3.56, 37.7) * mm, "end": v(-6.44, 32.7) * mm});
            skPoint(sketch, "E0.4.1.18", {"position": v(18.66, -38.1) * mm});
            skPoint(sketch, "E0.4.2.1", {"position": v(18.66, -32.32) * mm});
            skPoint(sketch, "E0.4.2.2", {"position": v(9.33, -37.7) * mm});
            skLineSegment(sketch, "E0.4.2.3", {"start": v(12.22, -32.7) * mm, "end": v(15.1, -37.7) * mm});
            skPoint(sketch, "E0.4.2.4", {"position": v(23.66, -29.43) * mm});
            skLineSegment(sketch, "E0.4.2.5", {"start": v(6.44, -32.7) * mm, "end": v(12.22, -32.7) * mm});
            skLineSegment(sketch, "E0.4.2.9", {"start": v(3.73, -38) * mm, "end": v(3.56, -37.7) * mm});
            skLineSegment(sketch, "E0.4.2.11", {"start": v(3.56, -37.7) * mm, "end": v(6.44, -32.7) * mm});
            skLineSegment(sketch, "E0.4.2.12", {"start": v(15.1, -37.7) * mm, "end": v(14.93, -38) * mm});
            skPoint(sketch, "E0.4.2.14", {"position": v(14.33, -34.82) * mm});
            skPoint(sketch, "E0.4.2.17", {"position": v(9.33, -32.7) * mm});
            skPoint(sketch, "E0.4.2.18", {"position": v(18.66, -27.32) * mm});
            skPoint(sketch, "E0.4.2.19", {"position": v(14.33, -34.82) * mm});
            skLineSegment(sketch, "E0.4.3.0", {"start": v(12.89, -21.55) * mm, "end": v(15.77, -16.55) * mm});
            skPoint(sketch, "E0.4.3.1", {"position": v(18.66, -21.55) * mm});
            skPoint(sketch, "E0.4.3.2", {"position": v(9.33, -26.93) * mm});
            skLineSegment(sketch, "E0.4.3.3", {"start": v(12.22, -21.93) * mm, "end": v(15.1, -26.93) * mm});
            skPoint(sketch, "E0.4.3.4", {"position": v(23.66, -18.66) * mm});
            skLineSegment(sketch, "E0.4.3.5", {"start": v(6.44, -21.93) * mm, "end": v(12.22, -21.93) * mm});
            skLineSegment(sketch, "E0.4.3.6", {"start": v(15.77, -16.55) * mm, "end": v(21.55, -16.55) * mm});
            skLineSegment(sketch, "E0.4.3.7", {"start": v(12.22, -31.93) * mm, "end": v(6.44, -31.93) * mm});
            skPoint(sketch, "E0.4.3.8", {"position": v(5, -29.43) * mm});
            skLineSegment(sketch, "E0.4.3.9", {"start": v(6.44, -31.93) * mm, "end": v(3.56, -26.93) * mm});
            skLineSegment(sketch, "E0.4.3.10", {"start": v(21.55, -16.55) * mm, "end": v(24.43, -21.55) * mm});
            skLineSegment(sketch, "E0.4.3.11", {"start": v(3.56, -26.93) * mm, "end": v(6.44, -21.93) * mm});
            skLineSegment(sketch, "E0.4.3.12", {"start": v(15.1, -26.93) * mm, "end": v(12.22, -31.93) * mm});
            skLineSegment(sketch, "E0.4.3.13", {"start": v(24.43, -21.55) * mm, "end": v(21.55, -26.55) * mm});
            skPoint(sketch, "E0.4.3.14", {"position": v(14.33, -24.05) * mm});
            skLineSegment(sketch, "E0.4.3.15", {"start": v(15.77, -26.55) * mm, "end": v(12.89, -21.55) * mm});
            skLineSegment(sketch, "E0.4.3.16", {"start": v(21.55, -26.55) * mm, "end": v(15.77, -26.55) * mm});
            skPoint(sketch, "E0.4.3.17", {"position": v(9.33, -21.93) * mm});
            skPoint(sketch, "E0.4.3.18", {"position": v(18.66, -16.55) * mm});
            skPoint(sketch, "E0.4.3.19", {"position": v(14.33, -24.05) * mm});
            skLineSegment(sketch, "E0.4.4.0", {"start": v(12.89, -10.77) * mm, "end": v(15.77, -5.77) * mm});
            skPoint(sketch, "E0.4.4.1", {"position": v(18.66, -10.77) * mm});
            skPoint(sketch, "E0.4.4.2", {"position": v(9.33, -16.16) * mm});
            skLineSegment(sketch, "E0.4.4.3", {"start": v(12.22, -11.16) * mm, "end": v(15.1, -16.16) * mm});
            skPoint(sketch, "E0.4.4.4", {"position": v(23.66, -7.89) * mm});
            skLineSegment(sketch, "E0.4.4.5", {"start": v(6.44, -11.16) * mm, "end": v(12.22, -11.16) * mm});
            skLineSegment(sketch, "E0.4.4.6", {"start": v(15.77, -5.77) * mm, "end": v(21.55, -5.77) * mm});
            skLineSegment(sketch, "E0.4.4.7", {"start": v(12.22, -21.16) * mm, "end": v(6.44, -21.16) * mm});
            skPoint(sketch, "E0.4.4.8", {"position": v(5, -18.66) * mm});
            skLineSegment(sketch, "E0.4.4.9", {"start": v(6.44, -21.16) * mm, "end": v(3.56, -16.16) * mm});
            skLineSegment(sketch, "E0.4.4.10", {"start": v(21.55, -5.77) * mm, "end": v(24.43, -10.77) * mm});
            skLineSegment(sketch, "E0.4.4.11", {"start": v(3.56, -16.16) * mm, "end": v(6.44, -11.16) * mm});
            skLineSegment(sketch, "E0.4.4.12", {"start": v(15.1, -16.16) * mm, "end": v(12.22, -21.16) * mm});
            skLineSegment(sketch, "E0.4.4.13", {"start": v(24.43, -10.77) * mm, "end": v(21.55, -15.77) * mm});
            skPoint(sketch, "E0.4.4.14", {"position": v(14.33, -13.27) * mm});
            skLineSegment(sketch, "E0.4.4.15", {"start": v(15.77, -15.77) * mm, "end": v(12.89, -10.77) * mm});
            skLineSegment(sketch, "E0.4.4.16", {"start": v(21.55, -15.77) * mm, "end": v(15.77, -15.77) * mm});
            skPoint(sketch, "E0.4.4.17", {"position": v(9.33, -11.16) * mm});
            skPoint(sketch, "E0.4.4.18", {"position": v(18.66, -5.77) * mm});
            skPoint(sketch, "E0.4.4.19", {"position": v(14.33, -13.27) * mm});
            skLineSegment(sketch, "E0.4.5.0", {"start": v(12.89, 0) * mm, "end": v(15.77, 5) * mm});
            skPoint(sketch, "E0.4.5.1", {"position": v(18.66, 0) * mm});
            skPoint(sketch, "E0.4.5.2", {"position": v(9.33, -5.39) * mm});
            skLineSegment(sketch, "E0.4.5.3", {"start": v(12.22, -0.39) * mm, "end": v(15.1, -5.39) * mm});
            skPoint(sketch, "E0.4.5.4", {"position": v(23.66, 2.89) * mm});
            skLineSegment(sketch, "E0.4.5.5", {"start": v(6.44, -0.39) * mm, "end": v(12.22, -0.39) * mm});
            skLineSegment(sketch, "E0.4.5.6", {"start": v(15.77, 5) * mm, "end": v(21.55, 5) * mm});
            skLineSegment(sketch, "E0.4.5.7", {"start": v(12.22, -10.39) * mm, "end": v(6.44, -10.39) * mm});
            skPoint(sketch, "E0.4.5.8", {"position": v(5, -7.89) * mm});
            skLineSegment(sketch, "E0.4.5.9", {"start": v(6.44, -10.39) * mm, "end": v(3.56, -5.39) * mm});
            skLineSegment(sketch, "E0.4.5.10", {"start": v(21.55, 5) * mm, "end": v(24.43, 0) * mm});
            skLineSegment(sketch, "E0.4.5.11", {"start": v(3.56, -5.39) * mm, "end": v(6.44, -0.39) * mm});
            skLineSegment(sketch, "E0.4.5.12", {"start": v(15.1, -5.39) * mm, "end": v(12.22, -10.39) * mm});
            skLineSegment(sketch, "E0.4.5.13", {"start": v(24.43, 0) * mm, "end": v(21.55, -5) * mm});
            skPoint(sketch, "E0.4.5.14", {"position": v(14.33, -2.5) * mm});
            skLineSegment(sketch, "E0.4.5.15", {"start": v(15.77, -5) * mm, "end": v(12.89, 0) * mm});
            skLineSegment(sketch, "E0.4.5.16", {"start": v(21.55, -5) * mm, "end": v(15.77, -5) * mm});
            skPoint(sketch, "E0.4.5.17", {"position": v(9.33, -0.39) * mm});
            skPoint(sketch, "E0.4.5.18", {"position": v(18.66, 5) * mm});
            skPoint(sketch, "E0.4.5.19", {"position": v(14.33, -2.5) * mm});
            skLineSegment(sketch, "E0.4.6.0", {"start": v(12.89, 10.77) * mm, "end": v(15.77, 15.77) * mm});
            skPoint(sketch, "E0.4.6.1", {"position": v(18.66, 10.77) * mm});
            skPoint(sketch, "E0.4.6.2", {"position": v(9.33, 5.39) * mm});
            skLineSegment(sketch, "E0.4.6.3", {"start": v(12.22, 10.39) * mm, "end": v(15.1, 5.39) * mm});
            skPoint(sketch, "E0.4.6.4", {"position": v(23.66, 13.66) * mm});
            skLineSegment(sketch, "E0.4.6.5", {"start": v(6.44, 10.39) * mm, "end": v(12.22, 10.39) * mm});
            skLineSegment(sketch, "E0.4.6.6", {"start": v(15.77, 15.77) * mm, "end": v(21.55, 15.77) * mm});
            skLineSegment(sketch, "E0.4.6.7", {"start": v(12.22, 0.39) * mm, "end": v(6.44, 0.39) * mm});
            skPoint(sketch, "E0.4.6.8", {"position": v(5, 2.89) * mm});
            skLineSegment(sketch, "E0.4.6.9", {"start": v(6.44, 0.39) * mm, "end": v(3.56, 5.39) * mm});
            skLineSegment(sketch, "E0.4.6.10", {"start": v(21.55, 15.77) * mm, "end": v(24.43, 10.77) * mm});
            skLineSegment(sketch, "E0.4.6.11", {"start": v(3.56, 5.39) * mm, "end": v(6.44, 10.39) * mm});
            skLineSegment(sketch, "E0.4.6.12", {"start": v(15.1, 5.39) * mm, "end": v(12.22, 0.39) * mm});
            skLineSegment(sketch, "E0.4.6.13", {"start": v(24.43, 10.77) * mm, "end": v(21.55, 5.77) * mm});
            skPoint(sketch, "E0.4.6.14", {"position": v(14.33, 8.27) * mm});
            skLineSegment(sketch, "E0.4.6.15", {"start": v(15.77, 5.77) * mm, "end": v(12.89, 10.77) * mm});
            skLineSegment(sketch, "E0.4.6.16", {"start": v(21.55, 5.77) * mm, "end": v(15.77, 5.77) * mm});
            skPoint(sketch, "E0.4.6.17", {"position": v(9.33, 10.39) * mm});
            skPoint(sketch, "E0.4.6.18", {"position": v(18.66, 15.77) * mm});
            skPoint(sketch, "E0.4.6.19", {"position": v(14.33, 8.27) * mm});
            skLineSegment(sketch, "E0.4.7.0", {"start": v(12.89, 21.55) * mm, "end": v(15.77, 26.55) * mm});
            skPoint(sketch, "E0.4.7.1", {"position": v(18.66, 21.55) * mm});
            skPoint(sketch, "E0.4.7.2", {"position": v(9.33, 16.16) * mm});
            skLineSegment(sketch, "E0.4.7.3", {"start": v(12.22, 21.16) * mm, "end": v(15.1, 16.16) * mm});
            skPoint(sketch, "E0.4.7.4", {"position": v(23.66, 24.43) * mm});
            skLineSegment(sketch, "E0.4.7.5", {"start": v(6.44, 21.16) * mm, "end": v(12.22, 21.16) * mm});
            skLineSegment(sketch, "E0.4.7.6", {"start": v(15.77, 26.55) * mm, "end": v(21.55, 26.55) * mm});
            skLineSegment(sketch, "E0.4.7.7", {"start": v(12.22, 11.16) * mm, "end": v(6.44, 11.16) * mm});
            skPoint(sketch, "E0.4.7.8", {"position": v(5, 13.66) * mm});
            skLineSegment(sketch, "E0.4.7.9", {"start": v(6.44, 11.16) * mm, "end": v(3.56, 16.16) * mm});
            skLineSegment(sketch, "E0.4.7.10", {"start": v(21.55, 26.55) * mm, "end": v(24.43, 21.55) * mm});
            skLineSegment(sketch, "E0.4.7.11", {"start": v(3.56, 16.16) * mm, "end": v(6.44, 21.16) * mm});
            skLineSegment(sketch, "E0.4.7.12", {"start": v(15.1, 16.16) * mm, "end": v(12.22, 11.16) * mm});
            skLineSegment(sketch, "E0.4.7.13", {"start": v(24.43, 21.55) * mm, "end": v(21.55, 16.55) * mm});
            skPoint(sketch, "E0.4.7.14", {"position": v(14.33, 19.05) * mm});
            skLineSegment(sketch, "E0.4.7.15", {"start": v(15.77, 16.55) * mm, "end": v(12.89, 21.55) * mm});
            skLineSegment(sketch, "E0.4.7.16", {"start": v(21.55, 16.55) * mm, "end": v(15.77, 16.55) * mm});
            skPoint(sketch, "E0.4.7.17", {"position": v(9.33, 21.16) * mm});
            skPoint(sketch, "E0.4.7.18", {"position": v(18.66, 26.55) * mm});
            skPoint(sketch, "E0.4.7.19", {"position": v(14.33, 19.05) * mm});
            skLineSegment(sketch, "E0.4.8.0", {"start": v(12.89, 32.32) * mm, "end": v(15.77, 37.32) * mm});
            skPoint(sketch, "E0.4.8.1", {"position": v(18.66, 32.32) * mm});
            skPoint(sketch, "E0.4.8.2", {"position": v(9.33, 26.93) * mm});
            skLineSegment(sketch, "E0.4.8.3", {"start": v(12.22, 31.93) * mm, "end": v(15.1, 26.93) * mm});
            skPoint(sketch, "E0.4.8.4", {"position": v(23.66, 35.2) * mm});
            skLineSegment(sketch, "E0.4.8.5", {"start": v(6.44, 31.93) * mm, "end": v(12.22, 31.93) * mm});
            skLineSegment(sketch, "E0.4.8.6", {"start": v(15.77, 37.32) * mm, "end": v(21.55, 37.32) * mm});
            skLineSegment(sketch, "E0.4.8.7", {"start": v(12.22, 21.93) * mm, "end": v(6.44, 21.93) * mm});
            skPoint(sketch, "E0.4.8.8", {"position": v(5, 24.43) * mm});
            skLineSegment(sketch, "E0.4.8.9", {"start": v(6.44, 21.93) * mm, "end": v(3.56, 26.93) * mm});
            skLineSegment(sketch, "E0.4.8.10", {"start": v(21.55, 37.32) * mm, "end": v(24.43, 32.32) * mm});
            skLineSegment(sketch, "E0.4.8.11", {"start": v(3.56, 26.93) * mm, "end": v(6.44, 31.93) * mm});
            skLineSegment(sketch, "E0.4.8.12", {"start": v(15.1, 26.93) * mm, "end": v(12.22, 21.93) * mm});
            skLineSegment(sketch, "E0.4.8.13", {"start": v(24.43, 32.32) * mm, "end": v(21.55, 27.32) * mm});
            skPoint(sketch, "E0.4.8.14", {"position": v(14.33, 29.82) * mm});
            skLineSegment(sketch, "E0.4.8.15", {"start": v(15.77, 27.32) * mm, "end": v(12.89, 32.32) * mm});
            skLineSegment(sketch, "E0.4.8.16", {"start": v(21.55, 27.32) * mm, "end": v(15.77, 27.32) * mm});
            skPoint(sketch, "E0.4.8.17", {"position": v(9.33, 31.93) * mm});
            skPoint(sketch, "E0.4.8.18", {"position": v(18.66, 37.32) * mm});
            skPoint(sketch, "E0.4.8.19", {"position": v(14.33, 29.82) * mm});
            skPoint(sketch, "E0.4.9.2", {"position": v(9.33, 37.7) * mm});
            skLineSegment(sketch, "E0.4.9.3", {"start": v(14.93, 38) * mm, "end": v(15.1, 37.7) * mm});
            skLineSegment(sketch, "E0.4.9.7", {"start": v(12.22, 32.7) * mm, "end": v(6.44, 32.7) * mm});
            skPoint(sketch, "E0.4.9.8", {"position": v(5, 35.2) * mm});
            skLineSegment(sketch, "E0.4.9.9", {"start": v(6.44, 32.7) * mm, "end": v(3.56, 37.7) * mm});
            skLineSegment(sketch, "E0.4.9.11", {"start": v(3.56, 37.7) * mm, "end": v(3.73, 38) * mm});
            skLineSegment(sketch, "E0.4.9.12", {"start": v(15.1, 37.7) * mm, "end": v(12.22, 32.7) * mm});
            skLineSegment(sketch, "E0.5.2.0", {"start": v(31.86, -31.78) * mm, "end": v(34.43, -27.32) * mm});
            skLineSegment(sketch, "E0.5.2.5", {"start": v(25.1, -32.7) * mm, "end": v(30.9, -32.7) * mm});
            skLineSegment(sketch, "E0.5.2.6", {"start": v(34.43, -27.32) * mm, "end": v(35.76, -27.32) * mm});
            skLineSegment(sketch, "E0.5.2.9", {"start": v(22.39, -38) * mm, "end": v(22.22, -37.7) * mm});
            skLineSegment(sketch, "E0.5.2.11", {"start": v(22.22, -37.7) * mm, "end": v(25.1, -32.7) * mm});
            skPoint(sketch, "E0.5.2.17", {"position": v(27.99, -32.7) * mm});
            skLineSegment(sketch, "E0.5.3.0", {"start": v(31.55, -21.55) * mm, "end": v(34.43, -16.55) * mm});
            skPoint(sketch, "E0.5.3.1", {"position": v(37.32, -21.55) * mm});
            skPoint(sketch, "E0.5.3.2", {"position": v(27.99, -26.93) * mm});
            skLineSegment(sketch, "E0.5.3.3", {"start": v(30.88, -21.93) * mm, "end": v(33.76, -26.93) * mm});
            skLineSegment(sketch, "E0.5.3.5", {"start": v(25.1, -21.93) * mm, "end": v(30.88, -21.93) * mm});
            skLineSegment(sketch, "E0.5.3.6", {"start": v(34.43, -16.55) * mm, "end": v(38, -16.55) * mm});
            skLineSegment(sketch, "E0.5.3.7", {"start": v(30.88, -31.93) * mm, "end": v(25.1, -31.93) * mm});
            skPoint(sketch, "E0.5.3.8", {"position": v(23.66, -29.43) * mm});
            skLineSegment(sketch, "E0.5.3.9", {"start": v(25.1, -31.93) * mm, "end": v(22.22, -26.93) * mm});
            skLineSegment(sketch, "E0.5.3.11", {"start": v(22.22, -26.93) * mm, "end": v(25.1, -21.93) * mm});
            skLineSegment(sketch, "E0.5.3.12", {"start": v(33.76, -26.93) * mm, "end": v(30.88, -31.93) * mm});
            skPoint(sketch, "E0.5.3.14", {"position": v(32.99, -24.05) * mm});
            skLineSegment(sketch, "E0.5.3.15", {"start": v(34.43, -26.55) * mm, "end": v(31.55, -21.55) * mm});
            skLineSegment(sketch, "E0.5.3.16", {"start": v(36.34, -26.55) * mm, "end": v(34.43, -26.55) * mm});
            skPoint(sketch, "E0.5.3.17", {"position": v(27.99, -21.93) * mm});
            skPoint(sketch, "E0.5.3.18", {"position": v(37.32, -16.55) * mm});
            skPoint(sketch, "E0.5.3.19", {"position": v(32.99, -24.05) * mm});
            skLineSegment(sketch, "E0.5.4.0", {"start": v(31.55, -10.77) * mm, "end": v(34.43, -5.77) * mm});
            skPoint(sketch, "E0.5.4.1", {"position": v(37.32, -10.77) * mm});
            skPoint(sketch, "E0.5.4.2", {"position": v(27.99, -16.16) * mm});
            skLineSegment(sketch, "E0.5.4.3", {"start": v(30.88, -11.16) * mm, "end": v(33.76, -16.16) * mm});
            skLineSegment(sketch, "E0.5.4.5", {"start": v(25.1, -11.16) * mm, "end": v(30.88, -11.16) * mm});
            skLineSegment(sketch, "E0.5.4.6", {"start": v(34.43, -5.77) * mm, "end": v(38, -5.77) * mm});
            skLineSegment(sketch, "E0.5.4.7", {"start": v(30.88, -21.16) * mm, "end": v(25.1, -21.16) * mm});
            skPoint(sketch, "E0.5.4.8", {"position": v(23.66, -18.66) * mm});
            skLineSegment(sketch, "E0.5.4.9", {"start": v(25.1, -21.16) * mm, "end": v(22.22, -16.16) * mm});
            skLineSegment(sketch, "E0.5.4.11", {"start": v(22.22, -16.16) * mm, "end": v(25.1, -11.16) * mm});
            skLineSegment(sketch, "E0.5.4.12", {"start": v(33.76, -16.16) * mm, "end": v(30.88, -21.16) * mm});
            skPoint(sketch, "E0.5.4.14", {"position": v(32.99, -13.27) * mm});
            skLineSegment(sketch, "E0.5.4.15", {"start": v(34.43, -15.77) * mm, "end": v(31.55, -10.77) * mm});
            skLineSegment(sketch, "E0.5.4.16", {"start": v(38, -15.77) * mm, "end": v(34.43, -15.77) * mm});
            skPoint(sketch, "E0.5.4.17", {"position": v(27.99, -11.16) * mm});
            skPoint(sketch, "E0.5.4.18", {"position": v(37.32, -5.77) * mm});
            skPoint(sketch, "E0.5.4.19", {"position": v(32.99, -13.27) * mm});
            skLineSegment(sketch, "E0.5.5.0", {"start": v(31.55, 0) * mm, "end": v(34.43, 5) * mm});
            skPoint(sketch, "E0.5.5.1", {"position": v(37.32, 0) * mm});
            skPoint(sketch, "E0.5.5.2", {"position": v(27.99, -5.39) * mm});
            skLineSegment(sketch, "E0.5.5.3", {"start": v(30.88, -0.39) * mm, "end": v(33.76, -5.39) * mm});
            skLineSegment(sketch, "E0.5.5.5", {"start": v(25.1, -0.39) * mm, "end": v(30.88, -0.39) * mm});
            skLineSegment(sketch, "E0.5.5.6", {"start": v(34.43, 5) * mm, "end": v(38, 5) * mm});
            skLineSegment(sketch, "E0.5.5.7", {"start": v(30.88, -10.39) * mm, "end": v(25.1, -10.39) * mm});
            skPoint(sketch, "E0.5.5.8", {"position": v(23.66, -7.89) * mm});
            skLineSegment(sketch, "E0.5.5.9", {"start": v(25.1, -10.39) * mm, "end": v(22.22, -5.39) * mm});
            skLineSegment(sketch, "E0.5.5.11", {"start": v(22.22, -5.39) * mm, "end": v(25.1, -0.39) * mm});
            skLineSegment(sketch, "E0.5.5.12", {"start": v(33.76, -5.39) * mm, "end": v(30.88, -10.39) * mm});
            skPoint(sketch, "E0.5.5.14", {"position": v(32.99, -2.5) * mm});
            skLineSegment(sketch, "E0.5.5.15", {"start": v(34.43, -5) * mm, "end": v(31.55, 0) * mm});
            skLineSegment(sketch, "E0.5.5.16", {"start": v(38, -5) * mm, "end": v(34.43, -5) * mm});
            skPoint(sketch, "E0.5.5.17", {"position": v(27.99, -0.39) * mm});
            skPoint(sketch, "E0.5.5.18", {"position": v(37.32, 5) * mm});
            skPoint(sketch, "E0.5.5.19", {"position": v(32.99, -2.5) * mm});
            skLineSegment(sketch, "E0.5.6.0", {"start": v(31.55, 10.77) * mm, "end": v(34.43, 15.77) * mm});
            skPoint(sketch, "E0.5.6.1", {"position": v(37.32, 10.77) * mm});
            skPoint(sketch, "E0.5.6.2", {"position": v(27.99, 5.39) * mm});
            skLineSegment(sketch, "E0.5.6.3", {"start": v(30.88, 10.39) * mm, "end": v(33.76, 5.39) * mm});
            skLineSegment(sketch, "E0.5.6.5", {"start": v(25.1, 10.39) * mm, "end": v(30.88, 10.39) * mm});
            skLineSegment(sketch, "E0.5.6.6", {"start": v(34.43, 15.77) * mm, "end": v(38, 15.77) * mm});
            skLineSegment(sketch, "E0.5.6.7", {"start": v(30.88, 0.39) * mm, "end": v(25.1, 0.39) * mm});
            skPoint(sketch, "E0.5.6.8", {"position": v(23.66, 2.89) * mm});
            skLineSegment(sketch, "E0.5.6.9", {"start": v(25.1, 0.39) * mm, "end": v(22.22, 5.39) * mm});
            skLineSegment(sketch, "E0.5.6.11", {"start": v(22.22, 5.39) * mm, "end": v(25.1, 10.39) * mm});
            skLineSegment(sketch, "E0.5.6.12", {"start": v(33.76, 5.39) * mm, "end": v(30.88, 0.39) * mm});
            skPoint(sketch, "E0.5.6.14", {"position": v(32.99, 8.27) * mm});
            skLineSegment(sketch, "E0.5.6.15", {"start": v(34.43, 5.77) * mm, "end": v(31.55, 10.77) * mm});
            skLineSegment(sketch, "E0.5.6.16", {"start": v(38, 5.77) * mm, "end": v(34.43, 5.77) * mm});
            skPoint(sketch, "E0.5.6.17", {"position": v(27.99, 10.39) * mm});
            skPoint(sketch, "E0.5.6.18", {"position": v(37.32, 15.77) * mm});
            skPoint(sketch, "E0.5.6.19", {"position": v(32.99, 8.27) * mm});
            skLineSegment(sketch, "E0.5.7.0", {"start": v(31.55, 21.55) * mm, "end": v(34.43, 26.55) * mm});
            skPoint(sketch, "E0.5.7.1", {"position": v(37.32, 21.55) * mm});
            skPoint(sketch, "E0.5.7.2", {"position": v(27.99, 16.16) * mm});
            skLineSegment(sketch, "E0.5.7.3", {"start": v(30.88, 21.16) * mm, "end": v(33.76, 16.16) * mm});
            skLineSegment(sketch, "E0.5.7.5", {"start": v(25.1, 21.16) * mm, "end": v(30.88, 21.16) * mm});
            skLineSegment(sketch, "E0.5.7.6", {"start": v(34.43, 26.55) * mm, "end": v(36.34, 26.55) * mm});
            skLineSegment(sketch, "E0.5.7.7", {"start": v(30.88, 11.16) * mm, "end": v(25.1, 11.16) * mm});
            skPoint(sketch, "E0.5.7.8", {"position": v(23.66, 13.66) * mm});
            skLineSegment(sketch, "E0.5.7.9", {"start": v(25.1, 11.16) * mm, "end": v(22.22, 16.16) * mm});
            skLineSegment(sketch, "E0.5.7.11", {"start": v(22.22, 16.16) * mm, "end": v(25.1, 21.16) * mm});
            skLineSegment(sketch, "E0.5.7.12", {"start": v(33.76, 16.16) * mm, "end": v(30.88, 11.16) * mm});
            skPoint(sketch, "E0.5.7.14", {"position": v(32.99, 19.05) * mm});
            skLineSegment(sketch, "E0.5.7.15", {"start": v(34.43, 16.55) * mm, "end": v(31.55, 21.55) * mm});
            skLineSegment(sketch, "E0.5.7.16", {"start": v(38, 16.55) * mm, "end": v(34.43, 16.55) * mm});
            skPoint(sketch, "E0.5.7.17", {"position": v(27.99, 21.16) * mm});
            skPoint(sketch, "E0.5.7.19", {"position": v(32.99, 19.05) * mm});
            skPoint(sketch, "E0.5.8.2", {"position": v(27.99, 26.93) * mm});
            skLineSegment(sketch, "E0.5.8.3", {"start": v(30.88, 31.93) * mm, "end": v(33.76, 26.93) * mm});
            skLineSegment(sketch, "E0.5.8.5", {"start": v(25.1, 31.93) * mm, "end": v(30.88, 31.93) * mm});
            skLineSegment(sketch, "E0.5.8.7", {"start": v(30.88, 21.93) * mm, "end": v(25.1, 21.93) * mm});
            skPoint(sketch, "E0.5.8.8", {"position": v(23.66, 24.43) * mm});
            skLineSegment(sketch, "E0.5.8.9", {"start": v(25.1, 21.93) * mm, "end": v(22.22, 26.93) * mm});
            skLineSegment(sketch, "E0.5.8.11", {"start": v(22.22, 26.93) * mm, "end": v(25.1, 31.93) * mm});
            skLineSegment(sketch, "E0.5.8.12", {"start": v(33.76, 26.93) * mm, "end": v(30.88, 21.93) * mm});
            skPoint(sketch, "E0.5.8.14", {"position": v(32.99, 29.82) * mm});
            skLineSegment(sketch, "E0.5.8.15", {"start": v(34.43, 27.32) * mm, "end": v(31.86, 31.78) * mm});
            skLineSegment(sketch, "E0.5.8.16", {"start": v(35.76, 27.32) * mm, "end": v(34.43, 27.32) * mm});
            skPoint(sketch, "E0.5.8.17", {"position": v(27.99, 31.93) * mm});
            skPoint(sketch, "E0.5.8.19", {"position": v(32.99, 29.82) * mm});
            skLineSegment(sketch, "E0.5.9.7", {"start": v(30.88, 32.7) * mm, "end": v(25.1, 32.7) * mm});
            skPoint(sketch, "E0.5.9.8", {"position": v(23.66, 35.2) * mm});
            skLineSegment(sketch, "E0.5.9.9", {"start": v(25.1, 32.7) * mm, "end": v(22.22, 37.7) * mm});
            skLineSegment(sketch, "E0.5.9.11", {"start": v(22.22, 37.7) * mm, "end": v(22.39, 38) * mm});
            skLineSegment(sketch, "E0.5.9.12", {"start": v(30.89, 32.73) * mm, "end": v(30.88, 32.7) * mm});
            skLineSegment(sketch, "E1.3.2.0", {"start": v(12.89, -32.32) * mm, "end": v(15.77, -27.32) * mm});
            skLineSegment(sketch, "E1.3.2.6", {"start": v(15.77, -27.32) * mm, "end": v(21.55, -27.32) * mm});
            skLineSegment(sketch, "E1.3.2.10", {"start": v(21.55, -27.32) * mm, "end": v(24.43, -32.32) * mm});
            skLineSegment(sketch, "E1.3.2.13", {"start": v(24.43, -32.32) * mm, "end": v(21.55, -37.32) * mm});
            skLineSegment(sketch, "E1.3.2.15", {"start": v(15.77, -37.32) * mm, "end": v(12.89, -32.32) * mm});
            skLineSegment(sketch, "E1.3.2.16", {"start": v(21.55, -37.32) * mm, "end": v(15.77, -37.32) * mm});
            skArc(sketch, "E2.trimOffspring", {"start": v(38, 24.1) * mm, "mid": v(37.19, 25.34) * mm, "end": v(36.34, 26.55) * mm});
            skArc(sketch, "E3.trimOffspring", {"start": v(-24.1, 38) * mm, "mid": v(-27.63, 35.52) * mm, "end": v(-30.9, 32.7) * mm});
            skArc(sketch, "E4.trimOffspring", {"start": v(30.89, 32.73) * mm, "mid": v(27.62, 35.53) * mm, "end": v(24.1, 38) * mm});
            skArc(sketch, "E5.trimOffspring", {"start": v(35.76, 27.32) * mm, "mid": v(33.88, 29.62) * mm, "end": v(31.86, 31.78) * mm});
            skArc(sketch, "E6.trimOffspring", {"start": v(36.34, -26.55) * mm, "mid": v(37.19, -25.34) * mm, "end": v(38, -24.1) * mm});
            skArc(sketch, "E7.trimOffspring", {"start": v(31.86, -31.78) * mm, "mid": v(33.88, -29.62) * mm, "end": v(35.76, -27.32) * mm});
            skArc(sketch, "E8.trimOffspring", {"start": v(24.1, -38) * mm, "mid": v(27.63, -35.52) * mm, "end": v(30.9, -32.7) * mm});
            skArc(sketch, "E9.trimOffspring", {"start": v(-30.9, -32.7) * mm, "mid": v(-27.63, -35.52) * mm, "end": v(-24.1, -38) * mm});
            skArc(sketch, "E10.trimOffspring", {"start": v(-35.76, -27.32) * mm, "mid": v(-33.88, -29.62) * mm, "end": v(-31.86, -31.78) * mm});
            skArc(sketch, "E11.trimOffspring", {"start": v(-38, -24.1) * mm, "mid": v(-37.19, -25.34) * mm, "end": v(-36.34, -26.55) * mm});
            skArc(sketch, "E12.trimOffspring", {"start": v(-31.86, 31.78) * mm, "mid": v(-33.88, 29.62) * mm, "end": v(-35.76, 27.32) * mm});
            skArc(sketch, "E13.trimOffspring", {"start": v(-36.34, 26.55) * mm, "mid": v(-37.19, 25.34) * mm, "end": v(-38, 24.1) * mm});
            skLineSegment(sketch, "E14.left", {"start": v(40, -40) * mm, "end": v(40, 43.5) * mm});
            skLineSegment(sketch, "E14.right", {"start": v(-40, -40) * mm, "end": v(-40, 43.5) * mm});
            skLineSegment(sketch, "E15.trimOffspring", {"start": v(40, -40) * mm, "end": v(-40, -40) * mm});
            skLineSegment(sketch, "E16", {"start": v(-42, 42) * mm, "end": v(42, -42) * mm, "construction": true});
            skLineSegment(sketch, "E17", {"start": v(42, 42) * mm, "end": v(-42, -42) * mm, "construction": true});
            skLineSegment(sketch, "E18.bottom", {"start": v(35.75, -35.75) * mm, "end": v(-35.75, -35.75) * mm, "construction": true});
            skLineSegment(sketch, "E18.top", {"start": v(35.75, 35.75) * mm, "end": v(-35.75, 35.75) * mm, "construction": true});
            skLineSegment(sketch, "E18.left", {"start": v(35.75, -35.75) * mm, "end": v(35.75, 35.75) * mm, "construction": true});
            skLineSegment(sketch, "E18.right", {"start": v(-35.75, -35.75) * mm, "end": v(-35.75, 35.75) * mm, "construction": true});
            skCircle(sketch, "E19", {"center": v(-35.75, 35.75) * mm, "radius": 2.5 * mm});
            skCircle(sketch, "E20", {"center": v(35.75, 35.75) * mm, "radius": 2.5 * mm});
            skPoint(sketch, "E21.visualSharp", {"position": v(-40, -40) * mm});
            skPoint(sketch, "E22.visualSharp", {"position": v(-40, 39.5) * mm});
            skPoint(sketch, "E23.visualSharp", {"position": v(40, -40) * mm});
            skLineSegment(sketch, "E24", {"start": v(-38, 24.1) * mm, "end": v(-38, 16.55) * mm});
            skLineSegment(sketch, "E25", {"start": v(-24.1, -38) * mm, "end": v(-22.39, -38) * mm});
            skLineSegment(sketch, "E26", {"start": v(38, -24.1) * mm, "end": v(38, -16.55) * mm});
            skLineSegment(sketch, "E27", {"start": v(24.1, 38) * mm, "end": v(22.39, 38) * mm});
            skLineSegment(sketch, "E28.trimOffspring", {"start": v(14.93, 38) * mm, "end": v(3.73, 38) * mm, "construction": true});
            skLineSegment(sketch, "E29.trimOffspring", {"start": v(-3.73, 38) * mm, "end": v(-14.93, 38) * mm, "construction": true});
            skLineSegment(sketch, "E30.trimOffspring", {"start": v(38, 5.77) * mm, "end": v(38, 15.77) * mm, "construction": true});
            skLineSegment(sketch, "E31.trimOffspring", {"start": v(-38, 15.77) * mm, "end": v(-38, 5.77) * mm});
            skLineSegment(sketch, "E32.trimOffspring", {"start": v(-38, 5) * mm, "end": v(-38, -5) * mm});
            skLineSegment(sketch, "E33.trimOffspring", {"start": v(-38, -5.77) * mm, "end": v(-38, -15.77) * mm});
            skLineSegment(sketch, "E34.trimOffspring", {"start": v(-38, -16.55) * mm, "end": v(-38, -24.1) * mm});
            skLineSegment(sketch, "E35.trimOffspring", {"start": v(-14.93, -38) * mm, "end": v(-3.73, -38) * mm});
            skLineSegment(sketch, "E36.trimOffspring", {"start": v(3.73, -38) * mm, "end": v(14.93, -38) * mm});
            skLineSegment(sketch, "E37.trimOffspring", {"start": v(22.39, -38) * mm, "end": v(24.1, -38) * mm});
            skLineSegment(sketch, "E38.trimOffspring", {"start": v(38, -15.77) * mm, "end": v(38, -5.77) * mm, "construction": true});
            skLineSegment(sketch, "E39.trimOffspring", {"start": v(38, -15.77) * mm, "end": v(38, -5.77) * mm});
            skLineSegment(sketch, "E40.trimOffspring", {"start": v(38, -5) * mm, "end": v(38, 5) * mm, "construction": true});
            skLineSegment(sketch, "E41.trimOffspring", {"start": v(38, 5.77) * mm, "end": v(38, 15.77) * mm});
            skLineSegment(sketch, "E42.trimOffspring", {"start": v(38, -5) * mm, "end": v(38, 5) * mm});
            skLineSegment(sketch, "E43.trimOffspring", {"start": v(38, 16.55) * mm, "end": v(38, 24.1) * mm});
            skLineSegment(sketch, "E44.trimOffspring", {"start": v(-22.39, 38) * mm, "end": v(-24.1, 38) * mm});
            skLineSegment(sketch, "E45.trimOffspring", {"start": v(-3.73, 38) * mm, "end": v(-14.93, 38) * mm});
            skLineSegment(sketch, "E46.trimOffspring", {"start": v(14.93, 38) * mm, "end": v(3.73, 38) * mm});
            skPoint(sketch, "E47", {"position": v(0, 43.5) * mm});
            skLineSegment(sketch, "E48", {"start": v(40, 43.5) * mm, "end": v(-40, 43.5) * mm});
            skLineSegment(sketch, "E49.MirrorCS", {"start": v(-40, -40) * mm, "end": v(40, -40) * mm});
            skLineSegment(sketch, "E50.MirrorCS", {"start": v(-40, 40) * mm, "end": v(40, 40) * mm, "construction": true});
            skSolve(sketch);
        }
        {
            var Q0;
            Q0=makeQuery(id+"F0.imprint","IMPRINT",FACE,{"disambiguationData":[TD([[makeQuery(id+"F0.imprint","IMPRINT",EDGE,{"derivedFrom":sQuery(id+"F0.wireOp",EDGE,"E0.1.2.6")}),1.0]])]});
            extrude(context, id + "F1", {"entities" : qUnion([Q0]), "depth" : 1.5 * mm, "offsetDistance" : 25 * mm});
        }
        {
            var Q0;
            Q0=makeQuery(id+"F1.opExtrude","CAP_FACE",FACE,{"disambiguationData":[OSD([sQuery(id+"F0.wireOp",EDGE,"E0.1.2.6"),sQuery(id+"F0.wireOp",EDGE,"E0.1.2.10"),sQuery(id+"F0.wireOp",EDGE,"E0.1.3.6"),sQuery(id+"F0.wireOp",EDGE,"E0.1.3.10"),sQuery(id+"F0.wireOp",EDGE,"E0.1.3.13"),sQuery(id+"F0.wireOp",EDGE,"E0.1.3.16"),sQuery(id+"F0.wireOp",EDGE,"E0.1.4.6"),sQuery(id+"F0.wireOp",EDGE,"E0.1.4.10"),sQuery(id+"F0.wireOp",EDGE,"E0.1.4.13"),sQuery(id+"F0.wireOp",EDGE,"E0.1.4.16"),sQuery(id+"F0.wireOp",EDGE,"E0.1.5.6"),sQuery(id+"F0.wireOp",EDGE,"E0.1.5.10"),sQuery(id+"F0.wireOp",EDGE,"E0.1.5.13"),sQuery(id+"F0.wireOp",EDGE,"E0.1.5.16"),sQuery(id+"F0.wireOp",EDGE,"E0.1.6.6"),sQuery(id+"F0.wireOp",EDGE,"E0.1.6.10"),sQuery(id+"F0.wireOp",EDGE,"E0.1.6.13"),sQuery(id+"F0.wireOp",EDGE,"E0.1.6.16"),sQuery(id+"F0.wireOp",EDGE,"E0.1.7.6"),sQuery(id+"F0.wireOp",EDGE,"E0.1.7.10"),sQuery(id+"F0.wireOp",EDGE,"E0.1.7.13"),sQuery(id+"F0.wireOp",EDGE,"E0.1.7.16"),sQuery(id+"F0.wireOp",EDGE,"E0.1.8.13"),sQuery(id+"F0.wireOp",EDGE,"E0.1.8.16"),sQuery(id+"F0.wireOp",EDGE,"E0.2.2.0"),sQuery(id+"F0.wireOp",EDGE,"E0.2.2.3"),sQuery(id+"F0.wireOp",EDGE,"E0.2.2.5"),sQuery(id+"F0.wireOp",EDGE,"E0.2.2.6"),sQuery(id+"F0.wireOp",EDGE,"E0.2.2.10"),sQuery(id+"F0.wireOp",EDGE,"E0.2.2.12"),sQuery(id+"F0.wireOp",EDGE,"E0.2.2.13"),sQuery(id+"F0.wireOp",EDGE,"E0.2.2.15"),sQuery(id+"F0.wireOp",EDGE,"E0.2.2.16"),sQuery(id+"F0.wireOp",EDGE,"E0.2.3.0"),sQuery(id+"F0.wireOp",EDGE,"E0.2.3.3"),sQuery(id+"F0.wireOp",EDGE,"E0.2.3.5"),sQuery(id+"F0.wireOp",EDGE,"E0.2.3.6"),sQuery(id+"F0.wireOp",EDGE,"E0.2.3.7"),sQuery(id+"F0.wireOp",EDGE,"E0.2.3.9"),sQuery(id+"F0.wireOp",EDGE,"E0.2.3.10"),sQuery(id+"F0.wireOp",EDGE,"E0.2.3.11"),sQuery(id+"F0.wireOp",EDGE,"E0.2.3.12"),sQuery(id+"F0.wireOp",EDGE,"E0.2.3.13"),sQuery(id+"F0.wireOp",EDGE,"E0.2.3.15"),sQuery(id+"F0.wireOp",EDGE,"E0.2.3.16"),sQuery(id+"F0.wireOp",EDGE,"E0.2.4.0"),sQuery(id+"F0.wireOp",EDGE,"E0.2.4.3"),sQuery(id+"F0.wireOp",EDGE,"E0.2.4.5"),sQuery(id+"F0.wireOp",EDGE,"E0.2.4.6"),sQuery(id+"F0.wireOp",EDGE,"E0.2.4.7"),sQuery(id+"F0.wireOp",EDGE,"E0.2.4.9"),sQuery(id+"F0.wireOp",EDGE,"E0.2.4.10"),sQuery(id+"F0.wireOp",EDGE,"E0.2.4.11"),sQuery(id+"F0.wireOp",EDGE,"E0.2.4.12"),sQuery(id+"F0.wireOp",EDGE,"E0.2.4.13"),sQuery(id+"F0.wireOp",EDGE,"E0.2.4.15"),sQuery(id+"F0.wireOp",EDGE,"E0.2.4.16"),sQuery(id+"F0.wireOp",EDGE,"E0.2.5.0"),sQuery(id+"F0.wireOp",EDGE,"E0.2.5.3"),sQuery(id+"F0.wireOp",EDGE,"E0.2.5.5"),sQuery(id+"F0.wireOp",EDGE,"E0.2.5.6"),sQuery(id+"F0.wireOp",EDGE,"E0.2.5.7"),sQuery(id+"F0.wireOp",EDGE,"E0.2.5.9"),sQuery(id+"F0.wireOp",EDGE,"E0.2.5.10"),sQuery(id+"F0.wireOp",EDGE,"E0.2.5.11"),sQuery(id+"F0.wireOp",EDGE,"E0.2.5.12"),sQuery(id+"F0.wireOp",EDGE,"E0.2.5.13"),sQuery(id+"F0.wireOp",EDGE,"E0.2.5.15"),sQuery(id+"F0.wireOp",EDGE,"E0.2.5.16"),sQuery(id+"F0.wireOp",EDGE,"E0.2.6.0"),sQuery(id+"F0.wireOp",EDGE,"E0.2.6.3"),sQuery(id+"F0.wireOp",EDGE,"E0.2.6.5"),sQuery(id+"F0.wireOp",EDGE,"E0.2.6.6"),sQuery(id+"F0.wireOp",EDGE,"E0.2.6.7"),sQuery(id+"F0.wireOp",EDGE,"E0.2.6.9"),sQuery(id+"F0.wireOp",EDGE,"E0.2.6.10"),sQuery(id+"F0.wireOp",EDGE,"E0.2.6.11"),sQuery(id+"F0.wireOp",EDGE,"E0.2.6.12"),sQuery(id+"F0.wireOp",EDGE,"E0.2.6.13"),sQuery(id+"F0.wireOp",EDGE,"E0.2.6.15"),sQuery(id+"F0.wireOp",EDGE,"E0.2.6.16"),sQuery(id+"F0.wireOp",EDGE,"E0.2.7.0"),sQuery(id+"F0.wireOp",EDGE,"E0.2.7.3"),sQuery(id+"F0.wireOp",EDGE,"E0.2.7.5"),sQuery(id+"F0.wireOp",EDGE,"E0.2.7.6"),sQuery(id+"F0.wireOp",EDGE,"E0.2.7.7"),sQuery(id+"F0.wireOp",EDGE,"E0.2.7.9"),sQuery(id+"F0.wireOp",EDGE,"E0.2.7.10"),sQuery(id+"F0.wireOp",EDGE,"E0.2.7.11"),sQuery(id+"F0.wireOp",EDGE,"E0.2.7.12"),sQuery(id+"F0.wireOp",EDGE,"E0.2.7.13"),sQuery(id+"F0.wireOp",EDGE,"E0.2.7.15"),sQuery(id+"F0.wireOp",EDGE,"E0.2.7.16"),sQuery(id+"F0.wireOp",EDGE,"E0.2.8.0"),sQuery(id+"F0.wireOp",EDGE,"E0.2.8.3"),sQuery(id+"F0.wireOp",EDGE,"E0.2.8.5"),sQuery(id+"F0.wireOp",EDGE,"E0.2.8.6"),sQuery(id+"F0.wireOp",EDGE,"E0.2.8.7"),sQuery(id+"F0.wireOp",EDGE,"E0.2.8.9"),sQuery(id+"F0.wireOp",EDGE,"E0.2.8.10"),sQuery(id+"F0.wireOp",EDGE,"E0.2.8.11"),sQuery(id+"F0.wireOp",EDGE,"E0.2.8.12"),sQuery(id+"F0.wireOp",EDGE,"E0.2.8.13"),sQuery(id+"F0.wireOp",EDGE,"E0.2.8.15"),sQuery(id+"F0.wireOp",EDGE,"E0.2.8.16"),sQuery(id+"F0.wireOp",EDGE,"E0.2.9.3"),sQuery(id+"F0.wireOp",EDGE,"E0.2.9.7"),sQuery(id+"F0.wireOp",EDGE,"E0.2.9.12"),sQuery(id+"F0.wireOp",EDGE,"E0.3.2.0"),sQuery(id+"F0.wireOp",EDGE,"E0.3.2.3"),sQuery(id+"F0.wireOp",EDGE,"E0.3.2.5"),sQuery(id+"F0.wireOp",EDGE,"E0.3.2.6"),sQuery(id+"F0.wireOp",EDGE,"E0.3.2.9"),sQuery(id+"F0.wireOp",EDGE,"E0.3.2.10"),sQuery(id+"F0.wireOp",EDGE,"E0.3.2.11"),sQuery(id+"F0.wireOp",EDGE,"E0.3.2.12"),sQuery(id+"F0.wireOp",EDGE,"E0.3.2.13"),sQuery(id+"F0.wireOp",EDGE,"E0.3.2.15"),sQuery(id+"F0.wireOp",EDGE,"E0.3.2.16"),sQuery(id+"F0.wireOp",EDGE,"E0.3.3.0"),sQuery(id+"F0.wireOp",EDGE,"E0.3.3.3"),sQuery(id+"F0.wireOp",EDGE,"E0.3.3.5"),sQuery(id+"F0.wireOp",EDGE,"E0.3.3.6"),sQuery(id+"F0.wireOp",EDGE,"E0.3.3.7"),sQuery(id+"F0.wireOp",EDGE,"E0.3.3.9"),sQuery(id+"F0.wireOp",EDGE,"E0.3.3.10"),sQuery(id+"F0.wireOp",EDGE,"E0.3.3.11"),sQuery(id+"F0.wireOp",EDGE,"E0.3.3.12"),sQuery(id+"F0.wireOp",EDGE,"E0.3.3.13"),sQuery(id+"F0.wireOp",EDGE,"E0.3.3.15"),sQuery(id+"F0.wireOp",EDGE,"E0.3.3.16"),sQuery(id+"F0.wireOp",EDGE,"E0.3.4.0"),sQuery(id+"F0.wireOp",EDGE,"E0.3.4.3"),sQuery(id+"F0.wireOp",EDGE,"E0.3.4.5"),sQuery(id+"F0.wireOp",EDGE,"E0.3.4.6"),sQuery(id+"F0.wireOp",EDGE,"E0.3.4.7"),sQuery(id+"F0.wireOp",EDGE,"E0.3.4.9"),sQuery(id+"F0.wireOp",EDGE,"E0.3.4.10"),sQuery(id+"F0.wireOp",EDGE,"E0.3.4.11"),sQuery(id+"F0.wireOp",EDGE,"E0.3.4.12"),sQuery(id+"F0.wireOp",EDGE,"E0.3.4.13"),sQuery(id+"F0.wireOp",EDGE,"E0.3.4.15"),sQuery(id+"F0.wireOp",EDGE,"E0.3.4.16"),sQuery(id+"F0.wireOp",EDGE,"E0.3.5.0"),sQuery(id+"F0.wireOp",EDGE,"E0.3.5.3"),sQuery(id+"F0.wireOp",EDGE,"E0.3.5.5"),sQuery(id+"F0.wireOp",EDGE,"E0.3.5.6"),sQuery(id+"F0.wireOp",EDGE,"E0.3.5.7"),sQuery(id+"F0.wireOp",EDGE,"E0.3.5.9"),sQuery(id+"F0.wireOp",EDGE,"E0.3.5.10"),sQuery(id+"F0.wireOp",EDGE,"E0.3.5.11"),sQuery(id+"F0.wireOp",EDGE,"E0.3.5.12"),sQuery(id+"F0.wireOp",EDGE,"E0.3.5.13"),sQuery(id+"F0.wireOp",EDGE,"E0.3.5.15"),sQuery(id+"F0.wireOp",EDGE,"E0.3.5.16"),sQuery(id+"F0.wireOp",EDGE,"E0.3.6.0"),sQuery(id+"F0.wireOp",EDGE,"E0.3.6.3"),sQuery(id+"F0.wireOp",EDGE,"E0.3.6.5"),sQuery(id+"F0.wireOp",EDGE,"E0.3.6.6"),sQuery(id+"F0.wireOp",EDGE,"E0.3.6.7"),sQuery(id+"F0.wireOp",EDGE,"E0.3.6.9"),sQuery(id+"F0.wireOp",EDGE,"E0.3.6.10"),sQuery(id+"F0.wireOp",EDGE,"E0.3.6.11"),sQuery(id+"F0.wireOp",EDGE,"E0.3.6.12"),sQuery(id+"F0.wireOp",EDGE,"E0.3.6.13"),sQuery(id+"F0.wireOp",EDGE,"E0.3.6.15"),sQuery(id+"F0.wireOp",EDGE,"E0.3.6.16"),sQuery(id+"F0.wireOp",EDGE,"E0.3.7.0"),sQuery(id+"F0.wireOp",EDGE,"E0.3.7.3"),sQuery(id+"F0.wireOp",EDGE,"E0.3.7.5"),sQuery(id+"F0.wireOp",EDGE,"E0.3.7.6"),sQuery(id+"F0.wireOp",EDGE,"E0.3.7.7"),sQuery(id+"F0.wireOp",EDGE,"E0.3.7.9"),sQuery(id+"F0.wireOp",EDGE,"E0.3.7.10"),sQuery(id+"F0.wireOp",EDGE,"E0.3.7.11"),sQuery(id+"F0.wireOp",EDGE,"E0.3.7.12"),sQuery(id+"F0.wireOp",EDGE,"E0.3.7.13"),sQuery(id+"F0.wireOp",EDGE,"E0.3.7.15"),sQuery(id+"F0.wireOp",EDGE,"E0.3.7.16"),sQuery(id+"F0.wireOp",EDGE,"E0.3.8.0"),sQuery(id+"F0.wireOp",EDGE,"E0.3.8.3"),sQuery(id+"F0.wireOp",EDGE,"E0.3.8.5"),sQuery(id+"F0.wireOp",EDGE,"E0.3.8.6"),sQuery(id+"F0.wireOp",EDGE,"E0.3.8.7"),sQuery(id+"F0.wireOp",EDGE,"E0.3.8.9"),sQuery(id+"F0.wireOp",EDGE,"E0.3.8.10"),sQuery(id+"F0.wireOp",EDGE,"E0.3.8.11"),sQuery(id+"F0.wireOp",EDGE,"E0.3.8.12"),sQuery(id+"F0.wireOp",EDGE,"E0.3.8.13"),sQuery(id+"F0.wireOp",EDGE,"E0.3.8.15"),sQuery(id+"F0.wireOp",EDGE,"E0.3.8.16"),sQuery(id+"F0.wireOp",EDGE,"E0.3.9.3"),sQuery(id+"F0.wireOp",EDGE,"E0.3.9.7"),sQuery(id+"F0.wireOp",EDGE,"E0.3.9.9"),sQuery(id+"F0.wireOp",EDGE,"E0.3.9.11"),sQuery(id+"F0.wireOp",EDGE,"E0.3.9.12"),sQuery(id+"F0.wireOp",EDGE,"E0.4.2.3"),sQuery(id+"F0.wireOp",EDGE,"E0.4.2.5"),sQuery(id+"F0.wireOp",EDGE,"E0.4.2.9"),sQuery(id+"F0.wireOp",EDGE,"E0.4.2.11"),sQuery(id+"F0.wireOp",EDGE,"E0.4.2.12"),sQuery(id+"F0.wireOp",EDGE,"E0.4.3.0"),sQuery(id+"F0.wireOp",EDGE,"E0.4.3.3"),sQuery(id+"F0.wireOp",EDGE,"E0.4.3.5"),sQuery(id+"F0.wireOp",EDGE,"E0.4.3.6"),sQuery(id+"F0.wireOp",EDGE,"E0.4.3.7"),sQuery(id+"F0.wireOp",EDGE,"E0.4.3.9"),sQuery(id+"F0.wireOp",EDGE,"E0.4.3.10"),sQuery(id+"F0.wireOp",EDGE,"E0.4.3.11"),sQuery(id+"F0.wireOp",EDGE,"E0.4.3.12"),sQuery(id+"F0.wireOp",EDGE,"E0.4.3.13"),sQuery(id+"F0.wireOp",EDGE,"E0.4.3.15"),sQuery(id+"F0.wireOp",EDGE,"E0.4.3.16"),sQuery(id+"F0.wireOp",EDGE,"E0.4.4.0"),sQuery(id+"F0.wireOp",EDGE,"E0.4.4.3"),sQuery(id+"F0.wireOp",EDGE,"E0.4.4.5"),sQuery(id+"F0.wireOp",EDGE,"E0.4.4.6"),sQuery(id+"F0.wireOp",EDGE,"E0.4.4.7"),sQuery(id+"F0.wireOp",EDGE,"E0.4.4.9"),sQuery(id+"F0.wireOp",EDGE,"E0.4.4.10"),sQuery(id+"F0.wireOp",EDGE,"E0.4.4.11"),sQuery(id+"F0.wireOp",EDGE,"E0.4.4.12"),sQuery(id+"F0.wireOp",EDGE,"E0.4.4.13"),sQuery(id+"F0.wireOp",EDGE,"E0.4.4.15"),sQuery(id+"F0.wireOp",EDGE,"E0.4.4.16"),sQuery(id+"F0.wireOp",EDGE,"E0.4.5.0"),sQuery(id+"F0.wireOp",EDGE,"E0.4.5.3"),sQuery(id+"F0.wireOp",EDGE,"E0.4.5.5"),sQuery(id+"F0.wireOp",EDGE,"E0.4.5.6"),sQuery(id+"F0.wireOp",EDGE,"E0.4.5.7"),sQuery(id+"F0.wireOp",EDGE,"E0.4.5.9"),sQuery(id+"F0.wireOp",EDGE,"E0.4.5.10"),sQuery(id+"F0.wireOp",EDGE,"E0.4.5.11"),sQuery(id+"F0.wireOp",EDGE,"E0.4.5.12"),sQuery(id+"F0.wireOp",EDGE,"E0.4.5.13"),sQuery(id+"F0.wireOp",EDGE,"E0.4.5.15"),sQuery(id+"F0.wireOp",EDGE,"E0.4.5.16"),sQuery(id+"F0.wireOp",EDGE,"E0.4.6.0"),sQuery(id+"F0.wireOp",EDGE,"E0.4.6.3"),sQuery(id+"F0.wireOp",EDGE,"E0.4.6.5"),sQuery(id+"F0.wireOp",EDGE,"E0.4.6.6"),sQuery(id+"F0.wireOp",EDGE,"E0.4.6.7"),sQuery(id+"F0.wireOp",EDGE,"E0.4.6.9"),sQuery(id+"F0.wireOp",EDGE,"E0.4.6.10"),sQuery(id+"F0.wireOp",EDGE,"E0.4.6.11"),sQuery(id+"F0.wireOp",EDGE,"E0.4.6.12"),sQuery(id+"F0.wireOp",EDGE,"E0.4.6.13"),sQuery(id+"F0.wireOp",EDGE,"E0.4.6.15"),sQuery(id+"F0.wireOp",EDGE,"E0.4.6.16"),sQuery(id+"F0.wireOp",EDGE,"E0.4.7.0"),sQuery(id+"F0.wireOp",EDGE,"E0.4.7.3"),sQuery(id+"F0.wireOp",EDGE,"E0.4.7.5"),sQuery(id+"F0.wireOp",EDGE,"E0.4.7.6"),sQuery(id+"F0.wireOp",EDGE,"E0.4.7.7"),sQuery(id+"F0.wireOp",EDGE,"E0.4.7.9"),sQuery(id+"F0.wireOp",EDGE,"E0.4.7.10"),sQuery(id+"F0.wireOp",EDGE,"E0.4.7.11"),sQuery(id+"F0.wireOp",EDGE,"E0.4.7.12"),sQuery(id+"F0.wireOp",EDGE,"E0.4.7.13"),sQuery(id+"F0.wireOp",EDGE,"E0.4.7.15"),sQuery(id+"F0.wireOp",EDGE,"E0.4.7.16"),sQuery(id+"F0.wireOp",EDGE,"E0.4.8.0"),sQuery(id+"F0.wireOp",EDGE,"E0.4.8.3"),sQuery(id+"F0.wireOp",EDGE,"E0.4.8.5"),sQuery(id+"F0.wireOp",EDGE,"E0.4.8.6"),sQuery(id+"F0.wireOp",EDGE,"E0.4.8.7"),sQuery(id+"F0.wireOp",EDGE,"E0.4.8.9"),sQuery(id+"F0.wireOp",EDGE,"E0.4.8.10"),sQuery(id+"F0.wireOp",EDGE,"E0.4.8.11"),sQuery(id+"F0.wireOp",EDGE,"E0.4.8.12"),sQuery(id+"F0.wireOp",EDGE,"E0.4.8.13"),sQuery(id+"F0.wireOp",EDGE,"E0.4.8.15"),sQuery(id+"F0.wireOp",EDGE,"E0.4.8.16"),sQuery(id+"F0.wireOp",EDGE,"E0.4.9.3"),sQuery(id+"F0.wireOp",EDGE,"E0.4.9.7"),sQuery(id+"F0.wireOp",EDGE,"E0.4.9.9"),sQuery(id+"F0.wireOp",EDGE,"E0.4.9.11"),sQuery(id+"F0.wireOp",EDGE,"E0.4.9.12"),sQuery(id+"F0.wireOp",EDGE,"E0.5.2.0"),sQuery(id+"F0.wireOp",EDGE,"E0.5.2.5"),sQuery(id+"F0.wireOp",EDGE,"E0.5.2.6"),sQuery(id+"F0.wireOp",EDGE,"E0.5.2.9"),sQuery(id+"F0.wireOp",EDGE,"E0.5.2.11"),sQuery(id+"F0.wireOp",EDGE,"E0.5.3.0"),sQuery(id+"F0.wireOp",EDGE,"E0.5.3.3"),sQuery(id+"F0.wireOp",EDGE,"E0.5.3.5"),sQuery(id+"F0.wireOp",EDGE,"E0.5.3.6"),sQuery(id+"F0.wireOp",EDGE,"E0.5.3.7"),sQuery(id+"F0.wireOp",EDGE,"E0.5.3.9"),sQuery(id+"F0.wireOp",EDGE,"E0.5.3.11"),sQuery(id+"F0.wireOp",EDGE,"E0.5.3.12"),sQuery(id+"F0.wireOp",EDGE,"E0.5.3.15"),sQuery(id+"F0.wireOp",EDGE,"E0.5.3.16"),sQuery(id+"F0.wireOp",EDGE,"E0.5.4.0"),sQuery(id+"F0.wireOp",EDGE,"E0.5.4.3"),sQuery(id+"F0.wireOp",EDGE,"E0.5.4.5"),sQuery(id+"F0.wireOp",EDGE,"E0.5.4.6"),sQuery(id+"F0.wireOp",EDGE,"E0.5.4.7"),sQuery(id+"F0.wireOp",EDGE,"E0.5.4.9"),sQuery(id+"F0.wireOp",EDGE,"E0.5.4.11"),sQuery(id+"F0.wireOp",EDGE,"E0.5.4.12"),sQuery(id+"F0.wireOp",EDGE,"E0.5.4.15"),sQuery(id+"F0.wireOp",EDGE,"E0.5.4.16"),sQuery(id+"F0.wireOp",EDGE,"E0.5.5.0"),sQuery(id+"F0.wireOp",EDGE,"E0.5.5.3"),sQuery(id+"F0.wireOp",EDGE,"E0.5.5.5"),sQuery(id+"F0.wireOp",EDGE,"E0.5.5.6"),sQuery(id+"F0.wireOp",EDGE,"E0.5.5.7"),sQuery(id+"F0.wireOp",EDGE,"E0.5.5.9"),sQuery(id+"F0.wireOp",EDGE,"E0.5.5.11"),sQuery(id+"F0.wireOp",EDGE,"E0.5.5.12"),sQuery(id+"F0.wireOp",EDGE,"E0.5.5.15"),sQuery(id+"F0.wireOp",EDGE,"E0.5.5.16"),sQuery(id+"F0.wireOp",EDGE,"E0.5.6.0"),sQuery(id+"F0.wireOp",EDGE,"E0.5.6.3"),sQuery(id+"F0.wireOp",EDGE,"E0.5.6.5"),sQuery(id+"F0.wireOp",EDGE,"E0.5.6.6"),sQuery(id+"F0.wireOp",EDGE,"E0.5.6.7"),sQuery(id+"F0.wireOp",EDGE,"E0.5.6.9"),sQuery(id+"F0.wireOp",EDGE,"E0.5.6.11"),sQuery(id+"F0.wireOp",EDGE,"E0.5.6.12"),sQuery(id+"F0.wireOp",EDGE,"E0.5.6.15"),sQuery(id+"F0.wireOp",EDGE,"E0.5.6.16"),sQuery(id+"F0.wireOp",EDGE,"E0.5.7.0"),sQuery(id+"F0.wireOp",EDGE,"E0.5.7.3"),sQuery(id+"F0.wireOp",EDGE,"E0.5.7.5"),sQuery(id+"F0.wireOp",EDGE,"E0.5.7.6"),sQuery(id+"F0.wireOp",EDGE,"E0.5.7.7"),sQuery(id+"F0.wireOp",EDGE,"E0.5.7.9"),sQuery(id+"F0.wireOp",EDGE,"E0.5.7.11"),sQuery(id+"F0.wireOp",EDGE,"E0.5.7.12"),sQuery(id+"F0.wireOp",EDGE,"E0.5.7.15"),sQuery(id+"F0.wireOp",EDGE,"E0.5.7.16"),sQuery(id+"F0.wireOp",EDGE,"E0.5.8.3"),sQuery(id+"F0.wireOp",EDGE,"E0.5.8.5"),sQuery(id+"F0.wireOp",EDGE,"E0.5.8.7"),sQuery(id+"F0.wireOp",EDGE,"E0.5.8.9"),sQuery(id+"F0.wireOp",EDGE,"E0.5.8.11"),sQuery(id+"F0.wireOp",EDGE,"E0.5.8.12"),sQuery(id+"F0.wireOp",EDGE,"E0.5.8.15"),sQuery(id+"F0.wireOp",EDGE,"E0.5.8.16"),sQuery(id+"F0.wireOp",EDGE,"E0.5.9.7"),sQuery(id+"F0.wireOp",EDGE,"E0.5.9.9"),sQuery(id+"F0.wireOp",EDGE,"E0.5.9.11"),sQuery(id+"F0.wireOp",EDGE,"E0.5.9.12"),sQuery(id+"F0.wireOp",EDGE,"E1.3.2.0"),sQuery(id+"F0.wireOp",EDGE,"E1.3.2.6"),sQuery(id+"F0.wireOp",EDGE,"E1.3.2.10"),sQuery(id+"F0.wireOp",EDGE,"E1.3.2.13"),sQuery(id+"F0.wireOp",EDGE,"E1.3.2.15"),sQuery(id+"F0.wireOp",EDGE,"E1.3.2.16"),sQuery(id+"F0.wireOp",EDGE,"E2.trimOffspring"),sQuery(id+"F0.wireOp",EDGE,"E3.trimOffspring"),sQuery(id+"F0.wireOp",EDGE,"E4.trimOffspring"),sQuery(id+"F0.wireOp",EDGE,"E5.trimOffspring"),sQuery(id+"F0.wireOp",EDGE,"E6.trimOffspring"),sQuery(id+"F0.wireOp",EDGE,"E7.trimOffspring"),sQuery(id+"F0.wireOp",EDGE,"E8.trimOffspring"),sQuery(id+"F0.wireOp",EDGE,"E9.trimOffspring"),sQuery(id+"F0.wireOp",EDGE,"E10.trimOffspring"),sQuery(id+"F0.wireOp",EDGE,"E11.trimOffspring"),sQuery(id+"F0.wireOp",EDGE,"E12.trimOffspring"),sQuery(id+"F0.wireOp",EDGE,"E13.trimOffspring"),sQuery(id+"F0.wireOp",EDGE,"E14.top"),sQuery(id+"F0.wireOp",EDGE,"E14.left"),sQuery(id+"F0.wireOp",EDGE,"E14.right"),sQuery(id+"F0.wireOp",EDGE,"E15.trimOffspring"),sQuery(id+"F0.wireOp",EDGE,"E19"),sQuery(id+"F0.wireOp",EDGE,"E20"),sQuery(id+"F0.wireOp",EDGE,"TNpwV9l6-fkPu-L3n3-qbS2-a2zZY725xSk5"),sQuery(id+"F0.wireOp",EDGE,"QaVxtbrI-aUlc-0ppP-Dtr5-awfs3sGSIKqW"),sQuery(id+"F0.wireOp",EDGE,"E21.filletArc"),sQuery(id+"F0.wireOp",EDGE,"E22.filletArc"),sQuery(id+"F0.wireOp",EDGE,"6d0acb84-fa23-4109-9f8c-01c58d766ffc.filletArc"),sQuery(id+"F0.wireOp",EDGE,"E23.filletArc"),sQuery(id+"F0.wireOp",EDGE,"E24"),sQuery(id+"F0.wireOp",EDGE,"E25"),sQuery(id+"F0.wireOp",EDGE,"E26"),sQuery(id+"F0.wireOp",EDGE,"E27"),sQuery(id+"F0.wireOp",EDGE,"E31.trimOffspring"),sQuery(id+"F0.wireOp",EDGE,"E32.trimOffspring"),sQuery(id+"F0.wireOp",EDGE,"E33.trimOffspring"),sQuery(id+"F0.wireOp",EDGE,"E34.trimOffspring"),sQuery(id+"F0.wireOp",EDGE,"E35.trimOffspring"),sQuery(id+"F0.wireOp",EDGE,"E36.trimOffspring"),sQuery(id+"F0.wireOp",EDGE,"E37.trimOffspring"),sQuery(id+"F0.wireOp",EDGE,"E39.trimOffspring"),sQuery(id+"F0.wireOp",EDGE,"E41.trimOffspring"),sQuery(id+"F0.wireOp",EDGE,"E42.trimOffspring"),sQuery(id+"F0.wireOp",EDGE,"E43.trimOffspring"),sQuery(id+"F0.wireOp",EDGE,"E44.trimOffspring"),sQuery(id+"F0.wireOp",EDGE,"E45.trimOffspring"),sQuery(id+"F0.wireOp",EDGE,"E46.trimOffspring")])],"isStart":false});
            var sketch = newSketch(context, id + "F2", { "sketchPlane" : qUnion([Q0])});
            skLineSegment(sketch, "E51.1", {"start": v(38, -24.1) * mm, "end": v(38, 24.1) * mm});
            skLineSegment(sketch, "E51.2", {"start": v(24.1, 38) * mm, "end": v(-24.1, 38) * mm});
            skLineSegment(sketch, "E51.7", {"start": v(24.1, -38) * mm, "end": v(-24.1, -38) * mm});
            skCircle(sketch, "E52.0", {"center": v(35.75, 35.75) * mm, "radius": 2.5 * mm});
            skCircle(sketch, "E53.0", {"center": v(-35.75, 35.75) * mm, "radius": 2.5 * mm});
            skLineSegment(sketch, "E54.trimOffspring", {"start": v(-38, -24.1) * mm, "end": v(-38, 24.1) * mm});
            skArc(sketch, "E55", {"start": v(-38, -24.1) * mm, "mid": v(-31.82, -31.82) * mm, "end": v(-24.1, -38) * mm});
            skArc(sketch, "E56.trimOffspring", {"start": v(-24.1, 38) * mm, "mid": v(-31.82, 31.82) * mm, "end": v(-38, 24.1) * mm});
            skArc(sketch, "E57.trimOffspring", {"start": v(38, 24.1) * mm, "mid": v(31.82, 31.82) * mm, "end": v(24.1, 38) * mm});
            skArc(sketch, "E58.trimOffspring", {"start": v(24.1, -38) * mm, "mid": v(31.82, -31.82) * mm, "end": v(38, -24.1) * mm});
            skLineSegment(sketch, "E59.0", {"start": v(-40, 40) * mm, "end": v(40, 40) * mm});
            skLineSegment(sketch, "E60.0", {"start": v(-40, -40) * mm, "end": v(40, -40) * mm});
            skLineSegment(sketch, "E60.1", {"start": v(-40, -40) * mm, "end": v(-40, 40) * mm});
            skLineSegment(sketch, "E60.2", {"start": v(40, -40) * mm, "end": v(40, 40) * mm});
            skPoint(sketch, "E61.orphan", {"position": v(-40, 43.5) * mm});
            skPoint(sketch, "E62.orphan", {"position": v(40, 43.5) * mm});
            skSolve(sketch);
        }
        {
            var Q0;
            Q0=makeQuery(id+"F2.imprint","IMPRINT",FACE,{"disambiguationData":[TD([[makeQuery(id+"F2.imprint","IMPRINT",EDGE,{"derivedFrom":sQuery(id+"F2.wireOp",EDGE,"E53.0")}),-1.0]])]});
            var Q1;
            {var subQ0=sQuery(id+"F2.wireOp",EDGE,"E59.0");Q1=makeQuery(id+"F2.imprint","IMPRINT",FACE,{"disambiguationData":[TD([[makeQuery(id+"F2.imprint","IMPRINT",EDGE,{"derivedFrom":subQ0}),1.0]])]});}
            extrude(context, id + "F3", {"entities" : qUnion([Q0, Q1]), "operationType" : NewBodyOperationType.ADD, "depth" : 1 * mm, "offsetDistance" : 25 * mm});
        }
        {
            var Q0;
            {var subQ0=sQuery(id+"F0.wireOp",EDGE,"E48");var subQ1=sQuery(id+"F0.wireOp",EDGE,"E14.right");Q0=makeQuery(id+"F3.boolean.opBoolean","MERGE",EDGE,{"derivedFrom":[makeQuery(id+"F1.opExtrude","SWEPT_EDGE",EDGE,{"disambiguationData":[OSD([subQ1,subQ0])]}),makeQuery(id+"F3.opExtrude","SWEPT_EDGE",EDGE,{"disambiguationData":[OSD([subQ1,subQ0])]})]});}
            var Q1;
            Q1=makeQuery(id+"F3.boolean.opBoolean","MERGE",EDGE,{"derivedFrom":[makeQuery(id+"F1.opExtrude","SWEPT_EDGE",EDGE,{"disambiguationData":[OSD([sQuery(id+"F0.wireOp",EDGE,"E14.right"),sQuery(id+"F0.wireOp",EDGE,"E49.MirrorCS")])]}),makeQuery(id+"F3.opExtrude","SWEPT_EDGE",EDGE,{"disambiguationData":[OSD([sQuery(id+"F2.wireOp",EDGE,"E60.0"),sQuery(id+"F2.wireOp",EDGE,"E60.1")])]})]});
            var Q2;
            Q2=makeQuery(id+"F3.boolean.opBoolean","MERGE",EDGE,{"derivedFrom":[makeQuery(id+"F1.opExtrude","SWEPT_EDGE",EDGE,{"disambiguationData":[OSD([sQuery(id+"F0.wireOp",EDGE,"E14.left"),sQuery(id+"F0.wireOp",EDGE,"E49.MirrorCS")])]}),makeQuery(id+"F3.opExtrude","SWEPT_EDGE",EDGE,{"disambiguationData":[OSD([sQuery(id+"F2.wireOp",EDGE,"E60.0"),sQuery(id+"F2.wireOp",EDGE,"E60.2")])]})]});
            var Q3;
            {var subQ0=sQuery(id+"F0.wireOp",EDGE,"E48");var subQ1=sQuery(id+"F0.wireOp",EDGE,"E14.left");Q3=makeQuery(id+"F3.boolean.opBoolean","MERGE",EDGE,{"derivedFrom":[makeQuery(id+"F1.opExtrude","SWEPT_EDGE",EDGE,{"disambiguationData":[OSD([subQ1,subQ0])]}),makeQuery(id+"F3.opExtrude","SWEPT_EDGE",EDGE,{"disambiguationData":[OSD([subQ1,subQ0])]})]});}
            fillet(context, id + "F4", {"entities" : qUnion([Q0, Q1, Q2, Q3]), "radius" : 6 * mm, "tangentPropagation" : true, "defaultsChanged" : true, "vertexSettings" : [], "allowEdgeOverflow" : false});
        }
    });
